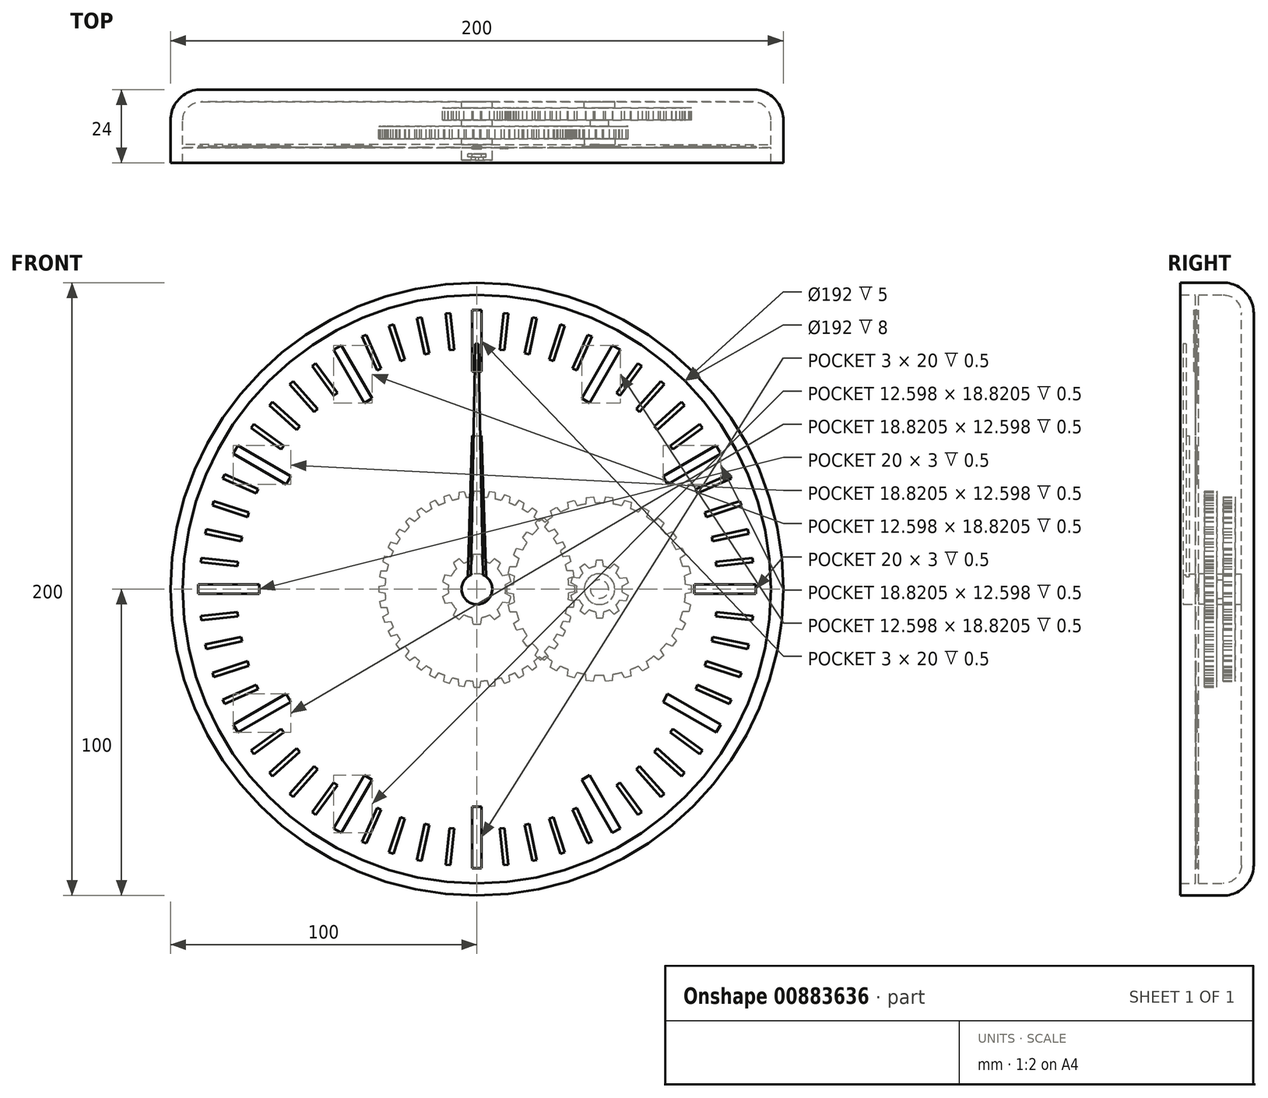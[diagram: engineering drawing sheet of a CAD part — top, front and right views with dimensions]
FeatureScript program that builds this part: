
annotation { "Feature Type Name" : "Feature", "Feature Type Description" : "" }
export const myFeature = defineFeature(function(context is Context, id is Id, definition is map)
    precondition{}
    {
        {
            var Q0;
            Q0=qCreatedBy(makeId("Front.planeOp"),FACE);
            var sketch = newSketch(context, id + "F0", { "sketchPlane" : qUnion([Q0])});
            skCircle(sketch, "E0", {"center": v(0, 0) * mm, "radius": 100 * mm});
            skSolve(sketch);
        }
        {
            var Q0;
            Q0=makeQuery(id+"F0.imprint","IMPRINT",FACE,{"disambiguationData":[TD([[makeQuery(id+"F0.imprint","IMPRINT",EDGE,{"derivedFrom":sQuery(id+"F0.wireOp",EDGE,"E0")}),1.0]])]});
            extrude(context, id + "F1", {"entities" : qUnion([Q0]), "depth" : 24 * mm, "offsetDistance" : 25 * mm});
        }
        {
            var Q0;
            Q0=makeQuery(id+"F1.opExtrude","CAP_EDGE",EDGE,{"disambiguationData":[OSD([sQuery(id+"F0.wireOp",EDGE,"E0")])],"isStart":true});
            fillet(context, id + "F2", {"entities" : qUnion([Q0]), "radius" : 10 * mm, "tangentPropagation" : true, "allowEdgeOverflow" : false});
        }
        {
            var Q0;
            Q0=makeQuery(id+"F1.opExtrude","CAP_FACE",FACE,{"disambiguationData":[OSD([sQuery(id+"F0.wireOp",EDGE,"E0")])],"isStart":false});
            shell(context, id + "F3", {"entities" : qUnion([Q0]), "thickness" : 4 * mm});
        }
        {
            var Q0;
            {var subQ0=sQuery(id+"F0.wireOp",EDGE,"E0");Q0=makeQuery(id+"F3.opShell","OFFSET_FACE",FACE,{"disambiguationData":[OSD([subQ0]),TDD([makeQuery(id+"F1.opExtrude","CAP_FACE",FACE,{"disambiguationData":[OSD([subQ0])],"isStart":true})])]});}
            var sketch = newSketch(context, id + "F4", { "sketchPlane" : qUnion([Q0])});
            skCircle(sketch, "E1", {"center": v(0, 0) * mm, "radius": 3 * mm});
            skCircle(sketch, "E2", {"center": v(0, 0) * mm, "radius": 5 * mm});
            skCircle(sketch, "E3", {"center": v(40, 0) * mm, "radius": 3 * mm});
            skCircle(sketch, "E4", {"center": v(40, 0) * mm, "radius": 5 * mm});
            skSolve(sketch);
        }
        {
            var Q0;
            Q0 = qSketchRegion(id + "F4", true);
            extrude(context, id + "F5", {"entities" : qUnion([Q0]), "operationType" : NewBodyOperationType.ADD, "depth" : 2 * mm, "offsetDistance" : 25 * mm});
        }
        {
            var Q0;
            {var subQ0=sQuery(id+"F0.wireOp",EDGE,"E0");Q0=makeQuery(id+"F5.boolean.opBoolean","SPLIT",FACE,{"disambiguationData":[TD([makeQuery(id+"F5.opExtrude","SWEPT_FACE",FACE,{"disambiguationData":[OSD([sQuery(id+"F4.wireOp",EDGE,"E1")])]})])],"derivedFrom":makeQuery(id+"F3.opShell","OFFSET_FACE",FACE,{"disambiguationData":[OSD([subQ0]),TDD([makeQuery(id+"F1.opExtrude","CAP_FACE",FACE,{"disambiguationData":[OSD([subQ0])],"isStart":true})])]})});}
            extrude(context, id + "F6", {"entities" : qUnion([Q0]), "depth" : 19 * mm, "offsetDistance" : 25 * mm});
        }
        {
            var Q0;
            {var subQ0=sQuery(id+"F0.wireOp",EDGE,"E0");Q0=makeQuery(id+"F5.boolean.opBoolean","SPLIT",FACE,{"disambiguationData":[TD([makeQuery(id+"F5.opExtrude","SWEPT_FACE",FACE,{"disambiguationData":[OSD([sQuery(id+"F4.wireOp",EDGE,"E3")])]})])],"derivedFrom":makeQuery(id+"F3.opShell","OFFSET_FACE",FACE,{"disambiguationData":[OSD([subQ0]),TDD([makeQuery(id+"F1.opExtrude","CAP_FACE",FACE,{"disambiguationData":[OSD([subQ0])],"isStart":true})])]})});}
            extrude(context, id + "F7", {"entities" : qUnion([Q0]), "depth" : 8 * mm, "offsetDistance" : 25 * mm});
        }
        {
            var Q0;
            Q0=makeQuery(id+"F5.opExtrude","CAP_FACE",FACE,{"disambiguationData":[OSD([sQuery(id+"F4.wireOp",EDGE,"E1"),sQuery(id+"F4.wireOp",EDGE,"E2")])],"isStart":false});
            var sketch = newSketch(context, id + "F8", { "sketchPlane" : qUnion([Q0])});
            skCircle(sketch, "E5", {"center": v(0, 0) * mm, "radius": 9.38 * mm});
            skLineSegment(sketch, "E6", {"start": v(0, 11.38) * mm, "end": v(1.18, 11.38) * mm});
            skLineSegment(sketch, "E7", {"start": v(1.18, 11.38) * mm, "end": v(1.55, 9.25) * mm});
            skLineSegment(sketch, "E8.MirrorCS", {"start": v(0, 11.38) * mm, "end": v(-1.18, 11.38) * mm});
            skLineSegment(sketch, "E9.MirrorCS", {"start": v(-1.18, 11.38) * mm, "end": v(-1.55, 9.25) * mm});
            skLineSegment(sketch, "E10.1.0", {"start": v(-7.64, 8.51) * mm, "end": v(-6.7, 6.57) * mm});
            skLineSegment(sketch, "E10.1.1", {"start": v(-6.69, 9.2) * mm, "end": v(-7.64, 8.51) * mm});
            skLineSegment(sketch, "E10.1.2", {"start": v(-6.69, 9.2) * mm, "end": v(-5.73, 9.9) * mm});
            skLineSegment(sketch, "E10.1.3", {"start": v(-5.73, 9.9) * mm, "end": v(-4.18, 8.4) * mm});
            skLineSegment(sketch, "E10.2.0", {"start": v(-11.18, 2.4) * mm, "end": v(-9.27, 1.38) * mm});
            skLineSegment(sketch, "E10.2.1", {"start": v(-10.82, 3.52) * mm, "end": v(-11.18, 2.4) * mm});
            skLineSegment(sketch, "E10.2.2", {"start": v(-10.82, 3.52) * mm, "end": v(-10.45, 4.64) * mm});
            skLineSegment(sketch, "E10.2.3", {"start": v(-10.45, 4.64) * mm, "end": v(-8.31, 4.33) * mm});
            skLineSegment(sketch, "E11.2.3.0", {"start": v(-10.45, -4.64) * mm, "end": v(-8.31, -4.33) * mm});
            skLineSegment(sketch, "E11.3.3.0", {"start": v(-10.82, -3.52) * mm, "end": v(-10.45, -4.64) * mm});
            skLineSegment(sketch, "E11.6.3.0", {"start": v(-10.82, -3.52) * mm, "end": v(-11.18, -2.4) * mm});
            skLineSegment(sketch, "E11.9.3.0", {"start": v(-11.18, -2.4) * mm, "end": v(-9.27, -1.38) * mm});
            skLineSegment(sketch, "E11.2.4.0", {"start": v(-5.73, -9.9) * mm, "end": v(-4.18, -8.4) * mm});
            skLineSegment(sketch, "E11.3.4.0", {"start": v(-6.69, -9.2) * mm, "end": v(-5.73, -9.9) * mm});
            skLineSegment(sketch, "E11.6.4.0", {"start": v(-6.69, -9.2) * mm, "end": v(-7.64, -8.51) * mm});
            skLineSegment(sketch, "E11.9.4.0", {"start": v(-7.64, -8.51) * mm, "end": v(-6.7, -6.57) * mm});
            skLineSegment(sketch, "E11.2.5.0", {"start": v(1.18, -11.38) * mm, "end": v(1.55, -9.25) * mm});
            skLineSegment(sketch, "E11.3.5.0", {"start": v(0, -11.38) * mm, "end": v(1.18, -11.38) * mm});
            skLineSegment(sketch, "E11.6.5.0", {"start": v(0, -11.38) * mm, "end": v(-1.18, -11.38) * mm});
            skLineSegment(sketch, "E11.9.5.0", {"start": v(-1.18, -11.38) * mm, "end": v(-1.55, -9.25) * mm});
            skLineSegment(sketch, "E11.2.6.0", {"start": v(7.64, -8.51) * mm, "end": v(6.7, -6.57) * mm});
            skLineSegment(sketch, "E11.3.6.0", {"start": v(6.69, -9.2) * mm, "end": v(7.64, -8.51) * mm});
            skLineSegment(sketch, "E11.6.6.0", {"start": v(6.69, -9.2) * mm, "end": v(5.73, -9.9) * mm});
            skLineSegment(sketch, "E11.9.6.0", {"start": v(5.73, -9.9) * mm, "end": v(4.18, -8.4) * mm});
            skLineSegment(sketch, "E11.2.7.0", {"start": v(11.18, -2.4) * mm, "end": v(9.27, -1.38) * mm});
            skLineSegment(sketch, "E11.3.7.0", {"start": v(10.82, -3.52) * mm, "end": v(11.18, -2.4) * mm});
            skLineSegment(sketch, "E11.6.7.0", {"start": v(10.82, -3.52) * mm, "end": v(10.45, -4.64) * mm});
            skLineSegment(sketch, "E11.9.7.0", {"start": v(10.45, -4.64) * mm, "end": v(8.31, -4.33) * mm});
            skLineSegment(sketch, "E11.2.8.0", {"start": v(10.45, 4.64) * mm, "end": v(8.31, 4.33) * mm});
            skLineSegment(sketch, "E11.3.8.0", {"start": v(10.82, 3.52) * mm, "end": v(10.45, 4.64) * mm});
            skLineSegment(sketch, "E11.6.8.0", {"start": v(10.82, 3.52) * mm, "end": v(11.18, 2.4) * mm});
            skLineSegment(sketch, "E11.9.8.0", {"start": v(11.18, 2.4) * mm, "end": v(9.27, 1.38) * mm});
            skLineSegment(sketch, "E11.2.9.0", {"start": v(5.73, 9.9) * mm, "end": v(4.18, 8.4) * mm});
            skLineSegment(sketch, "E11.3.9.0", {"start": v(6.69, 9.2) * mm, "end": v(5.73, 9.9) * mm});
            skLineSegment(sketch, "E11.6.9.0", {"start": v(6.69, 9.2) * mm, "end": v(7.64, 8.51) * mm});
            skLineSegment(sketch, "E11.9.9.0", {"start": v(7.64, 8.51) * mm, "end": v(6.7, 6.57) * mm});
            skSolve(sketch);
        }
        {
            var Q0;
            Q0 = qSketchRegion(id + "F8", true);
            extrude(context, id + "F9", {"entities" : qUnion([Q0]), "operationType" : NewBodyOperationType.ADD, "depth" : 4 * mm, "offsetDistance" : 25 * mm});
        }
        {
            var Q0;
            Q0=makeQuery(id+"F5.opExtrude","CAP_FACE",FACE,{"disambiguationData":[OSD([sQuery(id+"F4.wireOp",EDGE,"E3"),sQuery(id+"F4.wireOp",EDGE,"E4")])],"isStart":false});
            var sketch = newSketch(context, id + "F10", { "sketchPlane" : qUnion([Q0])});
            skCircle(sketch, "E12", {"center": v(40, 0) * mm, "radius": 28.12 * mm});
            skLineSegment(sketch, "E13", {"start": v(9.88, 0) * mm, "end": v(9.88, 1.18) * mm});
            skLineSegment(sketch, "E14", {"start": v(9.88, 1.18) * mm, "end": v(11.92, 1.54) * mm});
            skLineSegment(sketch, "E15.MirrorCS", {"start": v(9.88, 0) * mm, "end": v(9.88, -1.18) * mm});
            skLineSegment(sketch, "E16.MirrorCS", {"start": v(9.88, -1.18) * mm, "end": v(11.92, -1.54) * mm});
            skLineSegment(sketch, "E17.1.0", {"start": v(10.29, -5.11) * mm, "end": v(12.21, -4.33) * mm});
            skLineSegment(sketch, "E17.1.1", {"start": v(10.53, -6.26) * mm, "end": v(10.29, -5.11) * mm});
            skLineSegment(sketch, "E17.1.2", {"start": v(10.53, -6.26) * mm, "end": v(10.78, -7.42) * mm});
            skLineSegment(sketch, "E17.1.3", {"start": v(10.78, -7.42) * mm, "end": v(12.85, -7.34) * mm});
            skLineSegment(sketch, "E17.2.0", {"start": v(12, -11.18) * mm, "end": v(13.72, -10.02) * mm});
            skLineSegment(sketch, "E17.2.1", {"start": v(12.48, -12.25) * mm, "end": v(12, -11.18) * mm});
            skLineSegment(sketch, "E17.2.2", {"start": v(12.48, -12.25) * mm, "end": v(12.96, -13.33) * mm});
            skLineSegment(sketch, "E17.2.3", {"start": v(12.96, -13.33) * mm, "end": v(14.97, -12.83) * mm});
            skLineSegment(sketch, "E18.1.3.0", {"start": v(14.94, -16.75) * mm, "end": v(16.38, -15.26) * mm});
            skLineSegment(sketch, "E18.3.3.0", {"start": v(15.63, -17.7) * mm, "end": v(14.94, -16.75) * mm});
            skLineSegment(sketch, "E18.6.3.0", {"start": v(15.63, -17.7) * mm, "end": v(16.32, -18.66) * mm});
            skLineSegment(sketch, "E18.9.3.0", {"start": v(16.32, -18.66) * mm, "end": v(18.18, -17.75) * mm});
            skLineSegment(sketch, "E18.1.4.0", {"start": v(18.97, -21.6) * mm, "end": v(20.07, -19.84) * mm});
            skLineSegment(sketch, "E18.3.4.0", {"start": v(19.84, -22.39) * mm, "end": v(18.97, -21.6) * mm});
            skLineSegment(sketch, "E18.6.4.0", {"start": v(19.84, -22.39) * mm, "end": v(20.72, -23.18) * mm});
            skLineSegment(sketch, "E18.9.4.0", {"start": v(20.72, -23.18) * mm, "end": v(22.35, -21.9) * mm});
            skLineSegment(sketch, "E18.1.5.0", {"start": v(23.92, -25.5) * mm, "end": v(24.63, -23.55) * mm});
            skLineSegment(sketch, "E18.3.5.0", {"start": v(24.94, -26.09) * mm, "end": v(23.92, -25.5) * mm});
            skLineSegment(sketch, "E18.6.5.0", {"start": v(24.94, -26.09) * mm, "end": v(25.96, -26.68) * mm});
            skLineSegment(sketch, "E18.9.5.0", {"start": v(25.96, -26.68) * mm, "end": v(27.3, -25.09) * mm});
            skLineSegment(sketch, "E18.1.6.0", {"start": v(29.57, -28.29) * mm, "end": v(29.86, -26.23) * mm});
            skLineSegment(sketch, "E18.3.6.0", {"start": v(30.7, -28.65) * mm, "end": v(29.57, -28.29) * mm});
            skLineSegment(sketch, "E18.6.6.0", {"start": v(30.7, -28.65) * mm, "end": v(31.81, -29.01) * mm});
            skLineSegment(sketch, "E18.9.6.0", {"start": v(31.81, -29.01) * mm, "end": v(32.78, -27.18) * mm});
            skLineSegment(sketch, "E18.1.7.0", {"start": v(35.68, -29.84) * mm, "end": v(35.53, -27.77) * mm});
            skLineSegment(sketch, "E18.3.7.0", {"start": v(36.85, -29.96) * mm, "end": v(35.68, -29.84) * mm});
            skLineSegment(sketch, "E18.6.7.0", {"start": v(36.85, -29.96) * mm, "end": v(38.02, -30.08) * mm});
            skLineSegment(sketch, "E18.9.7.0", {"start": v(38.02, -30.08) * mm, "end": v(38.6, -28.09) * mm});
            skLineSegment(sketch, "E18.1.8.0", {"start": v(41.98, -30.08) * mm, "end": v(41.4, -28.09) * mm});
            skLineSegment(sketch, "E18.3.8.0", {"start": v(43.15, -29.96) * mm, "end": v(41.98, -30.08) * mm});
            skLineSegment(sketch, "E18.6.8.0", {"start": v(43.15, -29.96) * mm, "end": v(44.32, -29.84) * mm});
            skLineSegment(sketch, "E18.9.8.0", {"start": v(44.32, -29.84) * mm, "end": v(44.47, -27.77) * mm});
            skLineSegment(sketch, "E18.1.9.0", {"start": v(48.19, -29.01) * mm, "end": v(47.22, -27.18) * mm});
            skLineSegment(sketch, "E18.3.9.0", {"start": v(49.3, -28.65) * mm, "end": v(48.19, -29.01) * mm});
            skLineSegment(sketch, "E18.6.9.0", {"start": v(49.3, -28.65) * mm, "end": v(50.43, -28.29) * mm});
            skLineSegment(sketch, "E18.9.9.0", {"start": v(50.43, -28.29) * mm, "end": v(50.14, -26.23) * mm});
            skLineSegment(sketch, "E18.1.10.0", {"start": v(54.04, -26.68) * mm, "end": v(52.7, -25.09) * mm});
            skLineSegment(sketch, "E18.3.10.0", {"start": v(55.06, -26.09) * mm, "end": v(54.04, -26.68) * mm});
            skLineSegment(sketch, "E18.6.10.0", {"start": v(55.06, -26.09) * mm, "end": v(56.08, -25.5) * mm});
            skLineSegment(sketch, "E18.9.10.0", {"start": v(56.08, -25.5) * mm, "end": v(55.37, -23.55) * mm});
            skLineSegment(sketch, "E18.1.11.0", {"start": v(59.28, -23.18) * mm, "end": v(57.65, -21.9) * mm});
            skLineSegment(sketch, "E18.3.11.0", {"start": v(60.16, -22.39) * mm, "end": v(59.28, -23.18) * mm});
            skLineSegment(sketch, "E18.6.11.0", {"start": v(60.16, -22.39) * mm, "end": v(61.03, -21.6) * mm});
            skLineSegment(sketch, "E18.9.11.0", {"start": v(61.03, -21.6) * mm, "end": v(59.93, -19.84) * mm});
            skLineSegment(sketch, "E18.1.12.0", {"start": v(63.68, -18.66) * mm, "end": v(61.82, -17.75) * mm});
            skLineSegment(sketch, "E18.3.12.0", {"start": v(64.37, -17.7) * mm, "end": v(63.68, -18.66) * mm});
            skLineSegment(sketch, "E18.6.12.0", {"start": v(64.37, -17.7) * mm, "end": v(65.06, -16.75) * mm});
            skLineSegment(sketch, "E18.9.12.0", {"start": v(65.06, -16.75) * mm, "end": v(63.62, -15.26) * mm});
            skLineSegment(sketch, "E18.1.13.0", {"start": v(67.04, -13.33) * mm, "end": v(65.03, -12.83) * mm});
            skLineSegment(sketch, "E18.3.13.0", {"start": v(67.52, -12.25) * mm, "end": v(67.04, -13.33) * mm});
            skLineSegment(sketch, "E18.6.13.0", {"start": v(67.52, -12.25) * mm, "end": v(68, -11.18) * mm});
            skLineSegment(sketch, "E18.9.13.0", {"start": v(68, -11.18) * mm, "end": v(66.28, -10.02) * mm});
            skLineSegment(sketch, "E18.1.14.0", {"start": v(69.22, -7.42) * mm, "end": v(67.15, -7.34) * mm});
            skLineSegment(sketch, "E18.3.14.0", {"start": v(69.47, -6.26) * mm, "end": v(69.22, -7.42) * mm});
            skLineSegment(sketch, "E18.6.14.0", {"start": v(69.47, -6.26) * mm, "end": v(69.71, -5.11) * mm});
            skLineSegment(sketch, "E18.9.14.0", {"start": v(69.71, -5.11) * mm, "end": v(67.79, -4.33) * mm});
            skLineSegment(sketch, "E18.1.15.0", {"start": v(70.13, -1.18) * mm, "end": v(68.08, -1.54) * mm});
            skLineSegment(sketch, "E18.3.15.0", {"start": v(70.12, 0) * mm, "end": v(70.12, -1.18) * mm});
            skLineSegment(sketch, "E18.6.15.0", {"start": v(70.12, 0) * mm, "end": v(70.12, 1.18) * mm});
            skLineSegment(sketch, "E18.9.15.0", {"start": v(70.13, 1.18) * mm, "end": v(68.08, 1.54) * mm});
            skLineSegment(sketch, "E18.1.16.0", {"start": v(69.71, 5.11) * mm, "end": v(67.79, 4.33) * mm});
            skLineSegment(sketch, "E18.3.16.0", {"start": v(69.47, 6.26) * mm, "end": v(69.71, 5.11) * mm});
            skLineSegment(sketch, "E18.6.16.0", {"start": v(69.47, 6.26) * mm, "end": v(69.22, 7.42) * mm});
            skLineSegment(sketch, "E18.9.16.0", {"start": v(69.22, 7.42) * mm, "end": v(67.15, 7.34) * mm});
            skLineSegment(sketch, "E18.1.17.0", {"start": v(68, 11.18) * mm, "end": v(66.28, 10.02) * mm});
            skLineSegment(sketch, "E18.3.17.0", {"start": v(67.52, 12.25) * mm, "end": v(68, 11.18) * mm});
            skLineSegment(sketch, "E18.6.17.0", {"start": v(67.52, 12.25) * mm, "end": v(67.04, 13.33) * mm});
            skLineSegment(sketch, "E18.9.17.0", {"start": v(67.04, 13.33) * mm, "end": v(65.03, 12.83) * mm});
            skLineSegment(sketch, "E18.1.18.0", {"start": v(65.06, 16.75) * mm, "end": v(63.62, 15.26) * mm});
            skLineSegment(sketch, "E18.3.18.0", {"start": v(64.37, 17.7) * mm, "end": v(65.06, 16.75) * mm});
            skLineSegment(sketch, "E18.6.18.0", {"start": v(64.37, 17.7) * mm, "end": v(63.68, 18.66) * mm});
            skLineSegment(sketch, "E18.9.18.0", {"start": v(63.68, 18.66) * mm, "end": v(61.82, 17.75) * mm});
            skLineSegment(sketch, "E18.1.19.0", {"start": v(61.03, 21.6) * mm, "end": v(59.93, 19.84) * mm});
            skLineSegment(sketch, "E18.3.19.0", {"start": v(60.16, 22.39) * mm, "end": v(61.03, 21.6) * mm});
            skLineSegment(sketch, "E18.6.19.0", {"start": v(60.16, 22.39) * mm, "end": v(59.28, 23.18) * mm});
            skLineSegment(sketch, "E18.9.19.0", {"start": v(59.28, 23.18) * mm, "end": v(57.65, 21.9) * mm});
            skLineSegment(sketch, "E18.1.20.0", {"start": v(56.08, 25.5) * mm, "end": v(55.37, 23.55) * mm});
            skLineSegment(sketch, "E18.3.20.0", {"start": v(55.06, 26.09) * mm, "end": v(56.08, 25.5) * mm});
            skLineSegment(sketch, "E18.6.20.0", {"start": v(55.06, 26.09) * mm, "end": v(54.04, 26.68) * mm});
            skLineSegment(sketch, "E18.9.20.0", {"start": v(54.04, 26.68) * mm, "end": v(52.7, 25.09) * mm});
            skLineSegment(sketch, "E18.1.21.0", {"start": v(50.43, 28.29) * mm, "end": v(50.14, 26.23) * mm});
            skLineSegment(sketch, "E18.3.21.0", {"start": v(49.3, 28.65) * mm, "end": v(50.43, 28.29) * mm});
            skLineSegment(sketch, "E18.6.21.0", {"start": v(49.3, 28.65) * mm, "end": v(48.19, 29.01) * mm});
            skLineSegment(sketch, "E18.9.21.0", {"start": v(48.19, 29.01) * mm, "end": v(47.22, 27.18) * mm});
            skLineSegment(sketch, "E18.1.22.0", {"start": v(44.32, 29.84) * mm, "end": v(44.47, 27.77) * mm});
            skLineSegment(sketch, "E18.3.22.0", {"start": v(43.15, 29.96) * mm, "end": v(44.32, 29.84) * mm});
            skLineSegment(sketch, "E18.6.22.0", {"start": v(43.15, 29.96) * mm, "end": v(41.98, 30.08) * mm});
            skLineSegment(sketch, "E18.9.22.0", {"start": v(41.98, 30.08) * mm, "end": v(41.4, 28.09) * mm});
            skLineSegment(sketch, "E18.1.23.0", {"start": v(38.02, 30.08) * mm, "end": v(38.6, 28.09) * mm});
            skLineSegment(sketch, "E18.3.23.0", {"start": v(36.85, 29.96) * mm, "end": v(38.02, 30.08) * mm});
            skLineSegment(sketch, "E18.6.23.0", {"start": v(36.85, 29.96) * mm, "end": v(35.68, 29.84) * mm});
            skLineSegment(sketch, "E18.9.23.0", {"start": v(35.68, 29.84) * mm, "end": v(35.53, 27.77) * mm});
            skLineSegment(sketch, "E18.1.24.0", {"start": v(31.81, 29.01) * mm, "end": v(32.78, 27.18) * mm});
            skLineSegment(sketch, "E18.3.24.0", {"start": v(30.7, 28.65) * mm, "end": v(31.81, 29.01) * mm});
            skLineSegment(sketch, "E18.6.24.0", {"start": v(30.7, 28.65) * mm, "end": v(29.57, 28.29) * mm});
            skLineSegment(sketch, "E18.9.24.0", {"start": v(29.57, 28.29) * mm, "end": v(29.86, 26.23) * mm});
            skLineSegment(sketch, "E18.1.25.0", {"start": v(25.96, 26.68) * mm, "end": v(27.3, 25.09) * mm});
            skLineSegment(sketch, "E18.3.25.0", {"start": v(24.94, 26.09) * mm, "end": v(25.96, 26.68) * mm});
            skLineSegment(sketch, "E18.6.25.0", {"start": v(24.94, 26.09) * mm, "end": v(23.92, 25.5) * mm});
            skLineSegment(sketch, "E18.9.25.0", {"start": v(23.92, 25.5) * mm, "end": v(24.63, 23.55) * mm});
            skLineSegment(sketch, "E18.1.26.0", {"start": v(20.72, 23.18) * mm, "end": v(22.35, 21.9) * mm});
            skLineSegment(sketch, "E18.3.26.0", {"start": v(19.84, 22.39) * mm, "end": v(20.72, 23.18) * mm});
            skLineSegment(sketch, "E18.6.26.0", {"start": v(19.84, 22.39) * mm, "end": v(18.97, 21.6) * mm});
            skLineSegment(sketch, "E18.9.26.0", {"start": v(18.97, 21.6) * mm, "end": v(20.07, 19.84) * mm});
            skLineSegment(sketch, "E18.1.27.0", {"start": v(16.32, 18.66) * mm, "end": v(18.18, 17.75) * mm});
            skLineSegment(sketch, "E18.3.27.0", {"start": v(15.63, 17.7) * mm, "end": v(16.32, 18.66) * mm});
            skLineSegment(sketch, "E18.6.27.0", {"start": v(15.63, 17.7) * mm, "end": v(14.94, 16.75) * mm});
            skLineSegment(sketch, "E18.9.27.0", {"start": v(14.94, 16.75) * mm, "end": v(16.38, 15.26) * mm});
            skLineSegment(sketch, "E18.1.28.0", {"start": v(12.96, 13.33) * mm, "end": v(14.97, 12.83) * mm});
            skLineSegment(sketch, "E18.3.28.0", {"start": v(12.48, 12.25) * mm, "end": v(12.96, 13.33) * mm});
            skLineSegment(sketch, "E18.6.28.0", {"start": v(12.48, 12.25) * mm, "end": v(12, 11.18) * mm});
            skLineSegment(sketch, "E18.9.28.0", {"start": v(12, 11.18) * mm, "end": v(13.72, 10.02) * mm});
            skLineSegment(sketch, "E18.1.29.0", {"start": v(10.78, 7.42) * mm, "end": v(12.85, 7.34) * mm});
            skLineSegment(sketch, "E18.3.29.0", {"start": v(10.53, 6.26) * mm, "end": v(10.78, 7.42) * mm});
            skLineSegment(sketch, "E18.6.29.0", {"start": v(10.53, 6.26) * mm, "end": v(10.29, 5.11) * mm});
            skLineSegment(sketch, "E18.9.29.0", {"start": v(10.29, 5.11) * mm, "end": v(12.21, 4.33) * mm});
            skSolve(sketch);
        }
        {
            var Q0;
            Q0 = qSketchRegion(id + "F10", true);
            extrude(context, id + "F11", {"entities" : qUnion([Q0]), "operationType" : NewBodyOperationType.ADD, "depth" : 4 * mm, "offsetDistance" : 25 * mm});
        }
        {
            var Q0;
            Q0=makeQuery(id+"F9.opExtrude","CAP_FACE",FACE,{"disambiguationData":[OSD([sQuery(id+"F8.wireOp",EDGE,"E5"),sQuery(id+"F8.wireOp",EDGE,"E6"),sQuery(id+"F8.wireOp",EDGE,"E7"),sQuery(id+"F8.wireOp",EDGE,"E8.MirrorCS"),sQuery(id+"F8.wireOp",EDGE,"E9.MirrorCS"),sQuery(id+"F8.wireOp",EDGE,"E10.1.0"),sQuery(id+"F8.wireOp",EDGE,"E10.1.1"),sQuery(id+"F8.wireOp",EDGE,"E10.1.2"),sQuery(id+"F8.wireOp",EDGE,"E10.1.3"),sQuery(id+"F8.wireOp",EDGE,"E10.2.0"),sQuery(id+"F8.wireOp",EDGE,"E10.2.1"),sQuery(id+"F8.wireOp",EDGE,"E10.2.2"),sQuery(id+"F8.wireOp",EDGE,"E10.2.3"),sQuery(id+"F8.wireOp",EDGE,"E11.2.3.0"),sQuery(id+"F8.wireOp",EDGE,"E11.3.3.0"),sQuery(id+"F8.wireOp",EDGE,"E11.6.3.0"),sQuery(id+"F8.wireOp",EDGE,"E11.9.3.0"),sQuery(id+"F8.wireOp",EDGE,"E11.2.4.0"),sQuery(id+"F8.wireOp",EDGE,"E11.3.4.0"),sQuery(id+"F8.wireOp",EDGE,"E11.6.4.0"),sQuery(id+"F8.wireOp",EDGE,"E11.9.4.0"),sQuery(id+"F8.wireOp",EDGE,"E11.2.5.0"),sQuery(id+"F8.wireOp",EDGE,"E11.3.5.0"),sQuery(id+"F8.wireOp",EDGE,"E11.6.5.0"),sQuery(id+"F8.wireOp",EDGE,"E11.9.5.0"),sQuery(id+"F8.wireOp",EDGE,"E11.2.6.0"),sQuery(id+"F8.wireOp",EDGE,"E11.3.6.0"),sQuery(id+"F8.wireOp",EDGE,"E11.6.6.0"),sQuery(id+"F8.wireOp",EDGE,"E11.9.6.0"),sQuery(id+"F8.wireOp",EDGE,"E11.2.7.0"),sQuery(id+"F8.wireOp",EDGE,"E11.3.7.0"),sQuery(id+"F8.wireOp",EDGE,"E11.6.7.0"),sQuery(id+"F8.wireOp",EDGE,"E11.9.7.0"),sQuery(id+"F8.wireOp",EDGE,"E11.2.8.0"),sQuery(id+"F8.wireOp",EDGE,"E11.3.8.0"),sQuery(id+"F8.wireOp",EDGE,"E11.6.8.0"),sQuery(id+"F8.wireOp",EDGE,"E11.9.8.0"),sQuery(id+"F8.wireOp",EDGE,"E11.2.9.0"),sQuery(id+"F8.wireOp",EDGE,"E11.3.9.0"),sQuery(id+"F8.wireOp",EDGE,"E11.6.9.0"),sQuery(id+"F8.wireOp",EDGE,"E11.9.9.0")])],"isStart":false});
            var sketch = newSketch(context, id + "F12", { "sketchPlane" : qUnion([Q0])});
            skCircle(sketch, "E19.0", {"center": v(0, 0) * mm, "radius": 3 * mm});
            skCircle(sketch, "E20.0", {"center": v(0, 0) * mm, "radius": 5 * mm});
            skSolve(sketch);
        }
        {
            var Q0;
            Q0 = qSketchRegion(id + "F12", true);
            extrude(context, id + "F13", {"entities" : qUnion([Q0]), "depth" : 2 * mm, "offsetDistance" : 25 * mm});
        }
        {
            var Q0;
            Q0=makeQuery(id+"F13.opExtrude","CAP_FACE",FACE,{"disambiguationData":[OSD([sQuery(id+"F12.wireOp",EDGE,"E19.0"),sQuery(id+"F12.wireOp",EDGE,"E20.0")])],"isStart":false});
            var sketch = newSketch(context, id + "F14", { "sketchPlane" : qUnion([Q0])});
            skCircle(sketch, "E21.0", {"center": v(0, 0) * mm, "radius": 3 * mm});
            skCircle(sketch, "E22", {"center": v(0, 0) * mm, "radius": 30 * mm});
            skLineSegment(sketch, "E23", {"start": v(0, 32) * mm, "end": v(0.94, 32) * mm});
            skLineSegment(sketch, "E24", {"start": v(0.94, 32) * mm, "end": v(1.3, 29.97) * mm});
            skLineSegment(sketch, "E25.MirrorCS", {"start": v(0, 32) * mm, "end": v(-0.94, 32) * mm});
            skLineSegment(sketch, "E26.MirrorCS", {"start": v(-0.94, 32) * mm, "end": v(-1.3, 29.97) * mm});
            skLineSegment(sketch, "E27.1.0", {"start": v(-5.94, 31.46) * mm, "end": v(-5.97, 29.4) * mm});
            skLineSegment(sketch, "E27.1.1", {"start": v(-5, 31.6) * mm, "end": v(-5.94, 31.46) * mm});
            skLineSegment(sketch, "E27.1.2", {"start": v(-5, 31.6) * mm, "end": v(-4.08, 31.75) * mm});
            skLineSegment(sketch, "E27.1.3", {"start": v(-4.08, 31.75) * mm, "end": v(-3.4, 29.8) * mm});
            skLineSegment(sketch, "E27.2.0", {"start": v(-10.78, 30.14) * mm, "end": v(-10.5, 28.1) * mm});
            skLineSegment(sketch, "E27.2.1", {"start": v(-9.89, 30.43) * mm, "end": v(-10.78, 30.14) * mm});
            skLineSegment(sketch, "E27.2.2", {"start": v(-9.89, 30.43) * mm, "end": v(-9, 30.73) * mm});
            skLineSegment(sketch, "E27.2.3", {"start": v(-9, 30.73) * mm, "end": v(-8.03, 28.9) * mm});
            skLineSegment(sketch, "E28.2.3.0", {"start": v(-15.37, 28.08) * mm, "end": v(-14.77, 26.11) * mm});
            skLineSegment(sketch, "E28.3.3.0", {"start": v(-14.53, 28.51) * mm, "end": v(-15.37, 28.08) * mm});
            skLineSegment(sketch, "E28.6.3.0", {"start": v(-14.53, 28.51) * mm, "end": v(-13.69, 28.94) * mm});
            skLineSegment(sketch, "E28.9.3.0", {"start": v(-13.69, 28.94) * mm, "end": v(-12.45, 27.3) * mm});
            skLineSegment(sketch, "E28.2.4.0", {"start": v(-19.57, 25.33) * mm, "end": v(-18.67, 23.48) * mm});
            skLineSegment(sketch, "E28.3.4.0", {"start": v(-18.8, 25.89) * mm, "end": v(-19.57, 25.33) * mm});
            skLineSegment(sketch, "E28.6.4.0", {"start": v(-18.8, 25.89) * mm, "end": v(-18.05, 26.44) * mm});
            skLineSegment(sketch, "E28.9.4.0", {"start": v(-18.05, 26.44) * mm, "end": v(-16.57, 25.01) * mm});
            skLineSegment(sketch, "E28.2.5.0", {"start": v(-23.3, 21.96) * mm, "end": v(-22.11, 20.27) * mm});
            skLineSegment(sketch, "E28.3.5.0", {"start": v(-22.63, 22.63) * mm, "end": v(-23.3, 21.96) * mm});
            skLineSegment(sketch, "E28.6.5.0", {"start": v(-22.63, 22.63) * mm, "end": v(-21.96, 23.3) * mm});
            skLineSegment(sketch, "E28.9.5.0", {"start": v(-21.96, 23.3) * mm, "end": v(-20.27, 22.11) * mm});
            skLineSegment(sketch, "E28.2.6.0", {"start": v(-26.44, 18.05) * mm, "end": v(-25.01, 16.57) * mm});
            skLineSegment(sketch, "E28.3.6.0", {"start": v(-25.89, 18.8) * mm, "end": v(-26.44, 18.05) * mm});
            skLineSegment(sketch, "E28.6.6.0", {"start": v(-25.89, 18.8) * mm, "end": v(-25.33, 19.57) * mm});
            skLineSegment(sketch, "E28.9.6.0", {"start": v(-25.33, 19.57) * mm, "end": v(-23.48, 18.67) * mm});
            skLineSegment(sketch, "E28.2.7.0", {"start": v(-28.94, 13.69) * mm, "end": v(-27.3, 12.45) * mm});
            skLineSegment(sketch, "E28.3.7.0", {"start": v(-28.51, 14.53) * mm, "end": v(-28.94, 13.69) * mm});
            skLineSegment(sketch, "E28.6.7.0", {"start": v(-28.51, 14.53) * mm, "end": v(-28.08, 15.37) * mm});
            skLineSegment(sketch, "E28.9.7.0", {"start": v(-28.08, 15.37) * mm, "end": v(-26.11, 14.77) * mm});
            skLineSegment(sketch, "E28.2.8.0", {"start": v(-30.73, 9) * mm, "end": v(-28.9, 8.03) * mm});
            skLineSegment(sketch, "E28.3.8.0", {"start": v(-30.43, 9.89) * mm, "end": v(-30.73, 9) * mm});
            skLineSegment(sketch, "E28.6.8.0", {"start": v(-30.43, 9.89) * mm, "end": v(-30.14, 10.78) * mm});
            skLineSegment(sketch, "E28.9.8.0", {"start": v(-30.14, 10.78) * mm, "end": v(-28.1, 10.5) * mm});
            skLineSegment(sketch, "E28.2.9.0", {"start": v(-31.75, 4.08) * mm, "end": v(-29.8, 3.4) * mm});
            skLineSegment(sketch, "E28.3.9.0", {"start": v(-31.6, 5) * mm, "end": v(-31.75, 4.08) * mm});
            skLineSegment(sketch, "E28.6.9.0", {"start": v(-31.6, 5) * mm, "end": v(-31.46, 5.94) * mm});
            skLineSegment(sketch, "E28.9.9.0", {"start": v(-31.46, 5.94) * mm, "end": v(-29.4, 5.97) * mm});
            skLineSegment(sketch, "E28.2.10.0", {"start": v(-32, -0.94) * mm, "end": v(-29.97, -1.3) * mm});
            skLineSegment(sketch, "E28.3.10.0", {"start": v(-32, 0) * mm, "end": v(-32, -0.94) * mm});
            skLineSegment(sketch, "E28.6.10.0", {"start": v(-32, 0) * mm, "end": v(-32, 0.94) * mm});
            skLineSegment(sketch, "E28.9.10.0", {"start": v(-32, 0.94) * mm, "end": v(-29.97, 1.3) * mm});
            skLineSegment(sketch, "E28.2.11.0", {"start": v(-31.46, -5.94) * mm, "end": v(-29.4, -5.97) * mm});
            skLineSegment(sketch, "E28.3.11.0", {"start": v(-31.6, -5) * mm, "end": v(-31.46, -5.94) * mm});
            skLineSegment(sketch, "E28.6.11.0", {"start": v(-31.6, -5) * mm, "end": v(-31.75, -4.08) * mm});
            skLineSegment(sketch, "E28.9.11.0", {"start": v(-31.75, -4.08) * mm, "end": v(-29.8, -3.4) * mm});
            skLineSegment(sketch, "E28.2.12.0", {"start": v(-30.14, -10.78) * mm, "end": v(-28.1, -10.5) * mm});
            skLineSegment(sketch, "E28.3.12.0", {"start": v(-30.43, -9.89) * mm, "end": v(-30.14, -10.78) * mm});
            skLineSegment(sketch, "E28.6.12.0", {"start": v(-30.43, -9.89) * mm, "end": v(-30.73, -9) * mm});
            skLineSegment(sketch, "E28.9.12.0", {"start": v(-30.73, -9) * mm, "end": v(-28.9, -8.03) * mm});
            skLineSegment(sketch, "E28.2.13.0", {"start": v(-28.08, -15.37) * mm, "end": v(-26.11, -14.77) * mm});
            skLineSegment(sketch, "E28.3.13.0", {"start": v(-28.51, -14.53) * mm, "end": v(-28.08, -15.37) * mm});
            skLineSegment(sketch, "E28.6.13.0", {"start": v(-28.51, -14.53) * mm, "end": v(-28.94, -13.69) * mm});
            skLineSegment(sketch, "E28.9.13.0", {"start": v(-28.94, -13.69) * mm, "end": v(-27.3, -12.45) * mm});
            skLineSegment(sketch, "E28.2.14.0", {"start": v(-25.33, -19.57) * mm, "end": v(-23.48, -18.67) * mm});
            skLineSegment(sketch, "E28.3.14.0", {"start": v(-25.89, -18.8) * mm, "end": v(-25.33, -19.57) * mm});
            skLineSegment(sketch, "E28.6.14.0", {"start": v(-25.89, -18.8) * mm, "end": v(-26.44, -18.05) * mm});
            skLineSegment(sketch, "E28.9.14.0", {"start": v(-26.44, -18.05) * mm, "end": v(-25.01, -16.57) * mm});
            skLineSegment(sketch, "E28.2.15.0", {"start": v(-21.96, -23.3) * mm, "end": v(-20.27, -22.11) * mm});
            skLineSegment(sketch, "E28.3.15.0", {"start": v(-22.63, -22.63) * mm, "end": v(-21.96, -23.3) * mm});
            skLineSegment(sketch, "E28.6.15.0", {"start": v(-22.63, -22.63) * mm, "end": v(-23.3, -21.96) * mm});
            skLineSegment(sketch, "E28.9.15.0", {"start": v(-23.3, -21.96) * mm, "end": v(-22.11, -20.27) * mm});
            skLineSegment(sketch, "E28.2.16.0", {"start": v(-18.05, -26.44) * mm, "end": v(-16.57, -25.01) * mm});
            skLineSegment(sketch, "E28.3.16.0", {"start": v(-18.8, -25.89) * mm, "end": v(-18.05, -26.44) * mm});
            skLineSegment(sketch, "E28.6.16.0", {"start": v(-18.8, -25.89) * mm, "end": v(-19.57, -25.33) * mm});
            skLineSegment(sketch, "E28.9.16.0", {"start": v(-19.57, -25.33) * mm, "end": v(-18.67, -23.48) * mm});
            skLineSegment(sketch, "E28.2.17.0", {"start": v(-13.69, -28.94) * mm, "end": v(-12.45, -27.3) * mm});
            skLineSegment(sketch, "E28.3.17.0", {"start": v(-14.53, -28.51) * mm, "end": v(-13.69, -28.94) * mm});
            skLineSegment(sketch, "E28.6.17.0", {"start": v(-14.53, -28.51) * mm, "end": v(-15.37, -28.08) * mm});
            skLineSegment(sketch, "E28.9.17.0", {"start": v(-15.37, -28.08) * mm, "end": v(-14.77, -26.11) * mm});
            skLineSegment(sketch, "E28.2.18.0", {"start": v(-9, -30.73) * mm, "end": v(-8.03, -28.9) * mm});
            skLineSegment(sketch, "E28.3.18.0", {"start": v(-9.89, -30.43) * mm, "end": v(-9, -30.73) * mm});
            skLineSegment(sketch, "E28.6.18.0", {"start": v(-9.89, -30.43) * mm, "end": v(-10.78, -30.14) * mm});
            skLineSegment(sketch, "E28.9.18.0", {"start": v(-10.78, -30.14) * mm, "end": v(-10.5, -28.1) * mm});
            skLineSegment(sketch, "E28.2.19.0", {"start": v(-4.08, -31.75) * mm, "end": v(-3.4, -29.8) * mm});
            skLineSegment(sketch, "E28.3.19.0", {"start": v(-5, -31.6) * mm, "end": v(-4.08, -31.75) * mm});
            skLineSegment(sketch, "E28.6.19.0", {"start": v(-5, -31.6) * mm, "end": v(-5.94, -31.46) * mm});
            skLineSegment(sketch, "E28.9.19.0", {"start": v(-5.94, -31.46) * mm, "end": v(-5.97, -29.4) * mm});
            skLineSegment(sketch, "E28.2.20.0", {"start": v(0.94, -32) * mm, "end": v(1.3, -29.97) * mm});
            skLineSegment(sketch, "E28.3.20.0", {"start": v(0, -32) * mm, "end": v(0.94, -32) * mm});
            skLineSegment(sketch, "E28.6.20.0", {"start": v(0, -32) * mm, "end": v(-0.94, -32) * mm});
            skLineSegment(sketch, "E28.9.20.0", {"start": v(-0.94, -32) * mm, "end": v(-1.3, -29.97) * mm});
            skLineSegment(sketch, "E28.2.21.0", {"start": v(5.94, -31.46) * mm, "end": v(5.97, -29.4) * mm});
            skLineSegment(sketch, "E28.3.21.0", {"start": v(5, -31.6) * mm, "end": v(5.94, -31.46) * mm});
            skLineSegment(sketch, "E28.6.21.0", {"start": v(5, -31.6) * mm, "end": v(4.08, -31.75) * mm});
            skLineSegment(sketch, "E28.9.21.0", {"start": v(4.08, -31.75) * mm, "end": v(3.4, -29.8) * mm});
            skLineSegment(sketch, "E28.2.22.0", {"start": v(10.78, -30.14) * mm, "end": v(10.5, -28.1) * mm});
            skLineSegment(sketch, "E28.3.22.0", {"start": v(9.89, -30.43) * mm, "end": v(10.78, -30.14) * mm});
            skLineSegment(sketch, "E28.6.22.0", {"start": v(9.89, -30.43) * mm, "end": v(9, -30.73) * mm});
            skLineSegment(sketch, "E28.9.22.0", {"start": v(9, -30.73) * mm, "end": v(8.03, -28.9) * mm});
            skLineSegment(sketch, "E28.2.23.0", {"start": v(15.37, -28.08) * mm, "end": v(14.77, -26.11) * mm});
            skLineSegment(sketch, "E28.3.23.0", {"start": v(14.53, -28.51) * mm, "end": v(15.37, -28.08) * mm});
            skLineSegment(sketch, "E28.6.23.0", {"start": v(14.53, -28.51) * mm, "end": v(13.69, -28.94) * mm});
            skLineSegment(sketch, "E28.9.23.0", {"start": v(13.69, -28.94) * mm, "end": v(12.45, -27.3) * mm});
            skLineSegment(sketch, "E28.2.24.0", {"start": v(19.57, -25.33) * mm, "end": v(18.67, -23.48) * mm});
            skLineSegment(sketch, "E28.3.24.0", {"start": v(18.8, -25.89) * mm, "end": v(19.57, -25.33) * mm});
            skLineSegment(sketch, "E28.6.24.0", {"start": v(18.8, -25.89) * mm, "end": v(18.05, -26.44) * mm});
            skLineSegment(sketch, "E28.9.24.0", {"start": v(18.05, -26.44) * mm, "end": v(16.57, -25.01) * mm});
            skLineSegment(sketch, "E28.2.25.0", {"start": v(23.3, -21.96) * mm, "end": v(22.11, -20.27) * mm});
            skLineSegment(sketch, "E28.3.25.0", {"start": v(22.63, -22.63) * mm, "end": v(23.3, -21.96) * mm});
            skLineSegment(sketch, "E28.6.25.0", {"start": v(22.63, -22.63) * mm, "end": v(21.96, -23.3) * mm});
            skLineSegment(sketch, "E28.9.25.0", {"start": v(21.96, -23.3) * mm, "end": v(20.27, -22.11) * mm});
            skLineSegment(sketch, "E28.2.26.0", {"start": v(26.44, -18.05) * mm, "end": v(25.01, -16.57) * mm});
            skLineSegment(sketch, "E28.3.26.0", {"start": v(25.89, -18.8) * mm, "end": v(26.44, -18.05) * mm});
            skLineSegment(sketch, "E28.6.26.0", {"start": v(25.89, -18.8) * mm, "end": v(25.33, -19.57) * mm});
            skLineSegment(sketch, "E28.9.26.0", {"start": v(25.33, -19.57) * mm, "end": v(23.48, -18.67) * mm});
            skLineSegment(sketch, "E28.2.27.0", {"start": v(28.94, -13.69) * mm, "end": v(27.3, -12.45) * mm});
            skLineSegment(sketch, "E28.3.27.0", {"start": v(28.51, -14.53) * mm, "end": v(28.94, -13.69) * mm});
            skLineSegment(sketch, "E28.6.27.0", {"start": v(28.51, -14.53) * mm, "end": v(28.08, -15.37) * mm});
            skLineSegment(sketch, "E28.9.27.0", {"start": v(28.08, -15.37) * mm, "end": v(26.11, -14.77) * mm});
            skLineSegment(sketch, "E28.2.28.0", {"start": v(30.73, -9) * mm, "end": v(28.9, -8.03) * mm});
            skLineSegment(sketch, "E28.3.28.0", {"start": v(30.43, -9.89) * mm, "end": v(30.73, -9) * mm});
            skLineSegment(sketch, "E28.6.28.0", {"start": v(30.43, -9.89) * mm, "end": v(30.14, -10.78) * mm});
            skLineSegment(sketch, "E28.9.28.0", {"start": v(30.14, -10.78) * mm, "end": v(28.1, -10.5) * mm});
            skLineSegment(sketch, "E28.2.29.0", {"start": v(31.75, -4.08) * mm, "end": v(29.8, -3.4) * mm});
            skLineSegment(sketch, "E28.3.29.0", {"start": v(31.6, -5) * mm, "end": v(31.75, -4.08) * mm});
            skLineSegment(sketch, "E28.6.29.0", {"start": v(31.6, -5) * mm, "end": v(31.46, -5.94) * mm});
            skLineSegment(sketch, "E28.9.29.0", {"start": v(31.46, -5.94) * mm, "end": v(29.4, -5.97) * mm});
            skLineSegment(sketch, "E28.2.30.0", {"start": v(32, 0.94) * mm, "end": v(29.97, 1.3) * mm});
            skLineSegment(sketch, "E28.3.30.0", {"start": v(32, 0) * mm, "end": v(32, 0.94) * mm});
            skLineSegment(sketch, "E28.6.30.0", {"start": v(32, 0) * mm, "end": v(32, -0.94) * mm});
            skLineSegment(sketch, "E28.9.30.0", {"start": v(32, -0.94) * mm, "end": v(29.97, -1.3) * mm});
            skLineSegment(sketch, "E28.2.31.0", {"start": v(31.46, 5.94) * mm, "end": v(29.4, 5.97) * mm});
            skLineSegment(sketch, "E28.3.31.0", {"start": v(31.6, 5) * mm, "end": v(31.46, 5.94) * mm});
            skLineSegment(sketch, "E28.6.31.0", {"start": v(31.6, 5) * mm, "end": v(31.75, 4.08) * mm});
            skLineSegment(sketch, "E28.9.31.0", {"start": v(31.75, 4.08) * mm, "end": v(29.8, 3.4) * mm});
            skLineSegment(sketch, "E28.2.32.0", {"start": v(30.14, 10.78) * mm, "end": v(28.1, 10.5) * mm});
            skLineSegment(sketch, "E28.3.32.0", {"start": v(30.43, 9.89) * mm, "end": v(30.14, 10.78) * mm});
            skLineSegment(sketch, "E28.6.32.0", {"start": v(30.43, 9.89) * mm, "end": v(30.73, 9) * mm});
            skLineSegment(sketch, "E28.9.32.0", {"start": v(30.73, 9) * mm, "end": v(28.9, 8.03) * mm});
            skLineSegment(sketch, "E28.2.33.0", {"start": v(28.08, 15.37) * mm, "end": v(26.11, 14.77) * mm});
            skLineSegment(sketch, "E28.3.33.0", {"start": v(28.51, 14.53) * mm, "end": v(28.08, 15.37) * mm});
            skLineSegment(sketch, "E28.6.33.0", {"start": v(28.51, 14.53) * mm, "end": v(28.94, 13.69) * mm});
            skLineSegment(sketch, "E28.9.33.0", {"start": v(28.94, 13.69) * mm, "end": v(27.3, 12.45) * mm});
            skLineSegment(sketch, "E28.2.34.0", {"start": v(25.33, 19.57) * mm, "end": v(23.48, 18.67) * mm});
            skLineSegment(sketch, "E28.3.34.0", {"start": v(25.89, 18.8) * mm, "end": v(25.33, 19.57) * mm});
            skLineSegment(sketch, "E28.6.34.0", {"start": v(25.89, 18.8) * mm, "end": v(26.44, 18.05) * mm});
            skLineSegment(sketch, "E28.9.34.0", {"start": v(26.44, 18.05) * mm, "end": v(25.01, 16.57) * mm});
            skLineSegment(sketch, "E28.2.35.0", {"start": v(21.96, 23.3) * mm, "end": v(20.27, 22.11) * mm});
            skLineSegment(sketch, "E28.3.35.0", {"start": v(22.63, 22.63) * mm, "end": v(21.96, 23.3) * mm});
            skLineSegment(sketch, "E28.6.35.0", {"start": v(22.63, 22.63) * mm, "end": v(23.3, 21.96) * mm});
            skLineSegment(sketch, "E28.9.35.0", {"start": v(23.3, 21.96) * mm, "end": v(22.11, 20.27) * mm});
            skLineSegment(sketch, "E28.2.36.0", {"start": v(18.05, 26.44) * mm, "end": v(16.57, 25.01) * mm});
            skLineSegment(sketch, "E28.3.36.0", {"start": v(18.8, 25.89) * mm, "end": v(18.05, 26.44) * mm});
            skLineSegment(sketch, "E28.6.36.0", {"start": v(18.8, 25.89) * mm, "end": v(19.57, 25.33) * mm});
            skLineSegment(sketch, "E28.9.36.0", {"start": v(19.57, 25.33) * mm, "end": v(18.67, 23.48) * mm});
            skLineSegment(sketch, "E28.2.37.0", {"start": v(13.69, 28.94) * mm, "end": v(12.45, 27.3) * mm});
            skLineSegment(sketch, "E28.3.37.0", {"start": v(14.53, 28.51) * mm, "end": v(13.69, 28.94) * mm});
            skLineSegment(sketch, "E28.6.37.0", {"start": v(14.53, 28.51) * mm, "end": v(15.37, 28.08) * mm});
            skLineSegment(sketch, "E28.9.37.0", {"start": v(15.37, 28.08) * mm, "end": v(14.77, 26.11) * mm});
            skLineSegment(sketch, "E28.2.38.0", {"start": v(9, 30.73) * mm, "end": v(8.03, 28.9) * mm});
            skLineSegment(sketch, "E28.3.38.0", {"start": v(9.89, 30.43) * mm, "end": v(9, 30.73) * mm});
            skLineSegment(sketch, "E28.6.38.0", {"start": v(9.89, 30.43) * mm, "end": v(10.78, 30.14) * mm});
            skLineSegment(sketch, "E28.9.38.0", {"start": v(10.78, 30.14) * mm, "end": v(10.5, 28.1) * mm});
            skLineSegment(sketch, "E28.2.39.0", {"start": v(4.08, 31.75) * mm, "end": v(3.4, 29.8) * mm});
            skLineSegment(sketch, "E28.3.39.0", {"start": v(5, 31.6) * mm, "end": v(4.08, 31.75) * mm});
            skLineSegment(sketch, "E28.6.39.0", {"start": v(5, 31.6) * mm, "end": v(5.94, 31.46) * mm});
            skLineSegment(sketch, "E28.9.39.0", {"start": v(5.94, 31.46) * mm, "end": v(5.97, 29.4) * mm});
            skSolve(sketch);
        }
        {
            var Q0;
            Q0 = qSketchRegion(id + "F14", true);
            extrude(context, id + "F15", {"entities" : qUnion([Q0]), "operationType" : NewBodyOperationType.ADD, "depth" : 4 * mm, "offsetDistance" : 25 * mm});
        }
        {
            var Q0;
            Q0=makeQuery(id+"F7.opExtrude","CAP_FACE",FACE,{"disambiguationData":[OSD([sQuery(id+"F0.wireOp",EDGE,"E0")])],"isStart":false});
            var sketch = newSketch(context, id + "F16", { "sketchPlane" : qUnion([Q0])});
            skCircle(sketch, "E29", {"center": v(40, 0) * mm, "radius": 7.5 * mm});
            skLineSegment(sketch, "E30", {"start": v(40, 0) * mm, "end": v(40, 7.5) * mm, "construction": true});
            skLineSegment(sketch, "E31", {"start": v(38.68, 7.38) * mm, "end": v(39.06, 9.5) * mm});
            skLineSegment(sketch, "E32", {"start": v(39.06, 9.5) * mm, "end": v(40.94, 9.5) * mm});
            skLineSegment(sketch, "E33.MirrorCS", {"start": v(41.32, 7.38) * mm, "end": v(40.94, 9.5) * mm});
            skLineSegment(sketch, "E34.1.0", {"start": v(34.6, 5.2) * mm, "end": v(33.65, 7.13) * mm});
            skLineSegment(sketch, "E34.1.1", {"start": v(33.65, 7.13) * mm, "end": v(35.18, 8.24) * mm});
            skLineSegment(sketch, "E34.1.2", {"start": v(36.72, 6.75) * mm, "end": v(35.18, 8.24) * mm});
            skLineSegment(sketch, "E34.2.0", {"start": v(32.57, 1.03) * mm, "end": v(30.67, 2.04) * mm});
            skLineSegment(sketch, "E34.2.1", {"start": v(30.67, 2.04) * mm, "end": v(31.26, 3.83) * mm});
            skLineSegment(sketch, "E34.2.2", {"start": v(33.38, 3.53) * mm, "end": v(31.26, 3.83) * mm});
            skLineSegment(sketch, "E35.1.3.0", {"start": v(33.38, -3.53) * mm, "end": v(31.26, -3.83) * mm});
            skLineSegment(sketch, "E35.3.3.0", {"start": v(31.26, -3.83) * mm, "end": v(30.67, -2.04) * mm});
            skLineSegment(sketch, "E35.6.3.0", {"start": v(32.57, -1.03) * mm, "end": v(30.67, -2.04) * mm});
            skLineSegment(sketch, "E35.1.4.0", {"start": v(36.72, -6.75) * mm, "end": v(35.18, -8.24) * mm});
            skLineSegment(sketch, "E35.3.4.0", {"start": v(35.18, -8.24) * mm, "end": v(33.65, -7.13) * mm});
            skLineSegment(sketch, "E35.6.4.0", {"start": v(34.6, -5.2) * mm, "end": v(33.65, -7.13) * mm});
            skLineSegment(sketch, "E35.1.5.0", {"start": v(41.32, -7.38) * mm, "end": v(40.94, -9.5) * mm});
            skLineSegment(sketch, "E35.3.5.0", {"start": v(40.94, -9.5) * mm, "end": v(39.06, -9.5) * mm});
            skLineSegment(sketch, "E35.6.5.0", {"start": v(38.68, -7.38) * mm, "end": v(39.06, -9.5) * mm});
            skLineSegment(sketch, "E35.1.6.0", {"start": v(45.4, -5.2) * mm, "end": v(46.35, -7.13) * mm});
            skLineSegment(sketch, "E35.3.6.0", {"start": v(46.35, -7.13) * mm, "end": v(44.82, -8.24) * mm});
            skLineSegment(sketch, "E35.6.6.0", {"start": v(43.28, -6.75) * mm, "end": v(44.82, -8.24) * mm});
            skLineSegment(sketch, "E35.1.7.0", {"start": v(47.43, -1.03) * mm, "end": v(49.33, -2.04) * mm});
            skLineSegment(sketch, "E35.3.7.0", {"start": v(49.33, -2.04) * mm, "end": v(48.74, -3.83) * mm});
            skLineSegment(sketch, "E35.6.7.0", {"start": v(46.62, -3.53) * mm, "end": v(48.74, -3.83) * mm});
            skLineSegment(sketch, "E35.1.8.0", {"start": v(46.62, 3.53) * mm, "end": v(48.74, 3.83) * mm});
            skLineSegment(sketch, "E35.3.8.0", {"start": v(48.74, 3.83) * mm, "end": v(49.33, 2.04) * mm});
            skLineSegment(sketch, "E35.6.8.0", {"start": v(47.43, 1.03) * mm, "end": v(49.33, 2.04) * mm});
            skLineSegment(sketch, "E35.1.9.0", {"start": v(43.28, 6.75) * mm, "end": v(44.82, 8.24) * mm});
            skLineSegment(sketch, "E35.3.9.0", {"start": v(44.82, 8.24) * mm, "end": v(46.35, 7.13) * mm});
            skLineSegment(sketch, "E35.6.9.0", {"start": v(45.4, 5.2) * mm, "end": v(46.35, 7.13) * mm});
            skSolve(sketch);
        }
        {
            var Q0;
            Q0 = qSketchRegion(id + "F16", true);
            extrude(context, id + "F17", {"entities" : qUnion([Q0]), "operationType" : NewBodyOperationType.ADD, "depth" : 4 * mm, "offsetDistance" : 25 * mm});
        }
        {
            var Q0;
            Q0=makeQuery(id+"F17.opExtrude","CAP_FACE",FACE,{"disambiguationData":[OSD([sQuery(id+"F16.wireOp",EDGE,"E29"),sQuery(id+"F16.wireOp",EDGE,"E31"),sQuery(id+"F16.wireOp",EDGE,"E32"),sQuery(id+"F16.wireOp",EDGE,"E33.MirrorCS"),sQuery(id+"F16.wireOp",EDGE,"E34.1.0"),sQuery(id+"F16.wireOp",EDGE,"E34.1.1"),sQuery(id+"F16.wireOp",EDGE,"E34.1.2"),sQuery(id+"F16.wireOp",EDGE,"E34.2.0"),sQuery(id+"F16.wireOp",EDGE,"E34.2.1"),sQuery(id+"F16.wireOp",EDGE,"E34.2.2"),sQuery(id+"F16.wireOp",EDGE,"E35.1.3.0"),sQuery(id+"F16.wireOp",EDGE,"E35.3.3.0"),sQuery(id+"F16.wireOp",EDGE,"E35.6.3.0"),sQuery(id+"F16.wireOp",EDGE,"E35.1.4.0"),sQuery(id+"F16.wireOp",EDGE,"E35.3.4.0"),sQuery(id+"F16.wireOp",EDGE,"E35.6.4.0"),sQuery(id+"F16.wireOp",EDGE,"E35.1.5.0"),sQuery(id+"F16.wireOp",EDGE,"E35.3.5.0"),sQuery(id+"F16.wireOp",EDGE,"E35.6.5.0"),sQuery(id+"F16.wireOp",EDGE,"E35.1.6.0"),sQuery(id+"F16.wireOp",EDGE,"E35.3.6.0"),sQuery(id+"F16.wireOp",EDGE,"E35.6.6.0"),sQuery(id+"F16.wireOp",EDGE,"E35.1.7.0"),sQuery(id+"F16.wireOp",EDGE,"E35.3.7.0"),sQuery(id+"F16.wireOp",EDGE,"E35.6.7.0"),sQuery(id+"F16.wireOp",EDGE,"E35.1.8.0"),sQuery(id+"F16.wireOp",EDGE,"E35.3.8.0"),sQuery(id+"F16.wireOp",EDGE,"E35.6.8.0"),sQuery(id+"F16.wireOp",EDGE,"E35.1.9.0"),sQuery(id+"F16.wireOp",EDGE,"E35.3.9.0"),sQuery(id+"F16.wireOp",EDGE,"E35.6.9.0")])],"isStart":false});
            var sketch = newSketch(context, id + "F18", { "sketchPlane" : qUnion([Q0])});
            skCircle(sketch, "E36.0", {"center": v(40, 0) * mm, "radius": 3 * mm});
            skSolve(sketch);
        }
        {
            var Q0;
            Q0 = qSketchRegion(id + "F18", true);
            extrude(context, id + "F19", {"entities" : qUnion([Q0]), "operationType" : NewBodyOperationType.ADD, "depth" : 2 * mm, "offsetDistance" : 25 * mm});
        }
        {
            var Q0;
            Q0=makeQuery(id+"F19.opExtrude","CAP_FACE",FACE,{"disambiguationData":[OSD([sQuery(id+"F18.wireOp",EDGE,"E36.0")])],"isStart":false});
            var sketch = newSketch(context, id + "F20", { "sketchPlane" : qUnion([Q0])});
            skCircle(sketch, "E37", {"center": v(0, 0) * mm, "radius": 98 * mm});
            skCircle(sketch, "E38.0", {"center": v(0, 0) * mm, "radius": 5 * mm});
            skSolve(sketch);
        }
        {
            var Q0;
            Q0 = qSketchRegion(id + "F20", true);
            extrude(context, id + "F21", {"entities" : qUnion([Q0]), "depth" : 1 * mm, "offsetDistance" : 25 * mm});
        }
        {
            var Q0;
            Q0=makeQuery(id+"F21.opExtrude","SWEPT_BODY",BODY,{"disambiguationData":[OSD([sQuery(id+"F20.wireOp",EDGE,"E37"),sQuery(id+"F20.wireOp",EDGE,"E38.0")])]});
            var Q1;
            Q1=makeQuery(id+"F1.opExtrude","SWEPT_BODY",BODY,{"disambiguationData":[OSD([sQuery(id+"F0.wireOp",EDGE,"E0")])]});
            booleanBodies(context, id + "F22", {"operationType" : BooleanOperationType.SUBTRACTION, "tools" : qUnion([Q0]), "targets" : qUnion([Q1]), "keepTools" : true});
        }
        {
            var Q0;
            Q0=makeQuery(id+"F21.opExtrude","CAP_FACE",FACE,{"disambiguationData":[OSD([sQuery(id+"F20.wireOp",EDGE,"E37"),sQuery(id+"F20.wireOp",EDGE,"E38.0")])],"isStart":true});
            var sketch = newSketch(context, id + "F23", { "sketchPlane" : qUnion([Q0])});
            skCircle(sketch, "E39.0", {"center": v(-40, 0) * mm, "radius": 3 * mm});
            skCircle(sketch, "E40", {"center": v(-40, 0) * mm, "radius": 5 * mm});
            skSolve(sketch);
        }
        {
            var Q0;
            Q0 = qSketchRegion(id + "F23", true);
            extrude(context, id + "F24", {"entities" : qUnion([Q0]), "operationType" : NewBodyOperationType.ADD, "endBound" : BoundingType.UP_TO_NEXT, "depth" : 25 * mm, "offsetDistance" : 25 * mm});
        }
        {
            var Q0;
            Q0=makeQuery(id+"F21.opExtrude","CAP_FACE",FACE,{"disambiguationData":[OSD([sQuery(id+"F20.wireOp",EDGE,"E37"),sQuery(id+"F20.wireOp",EDGE,"E38.0")])],"isStart":false});
            var sketch = newSketch(context, id + "F25", { "sketchPlane" : qUnion([Q0])});
            skLineSegment(sketch, "E41.bottom", {"start": v(1.5, 71) * mm, "end": v(-1.5, 71) * mm});
            skLineSegment(sketch, "E41.top", {"start": v(1.5, 91) * mm, "end": v(-1.5, 91) * mm});
            skLineSegment(sketch, "E41.left", {"start": v(1.5, 71) * mm, "end": v(1.5, 91) * mm});
            skLineSegment(sketch, "E41.right", {"start": v(-1.5, 71) * mm, "end": v(-1.5, 91) * mm});
            skPoint(sketch, "E41.middle", {"position": v(0, 81) * mm});
            skLineSegment(sketch, "E42.1.0", {"start": v(-36.8, 60.74) * mm, "end": v(-46.8, 78.06) * mm});
            skLineSegment(sketch, "E42.1.1", {"start": v(-44.2, 79.56) * mm, "end": v(-46.8, 78.06) * mm});
            skLineSegment(sketch, "E42.1.2", {"start": v(-34.2, 62.24) * mm, "end": v(-44.2, 79.56) * mm});
            skLineSegment(sketch, "E42.1.3", {"start": v(-34.2, 62.24) * mm, "end": v(-36.8, 60.74) * mm});
            skLineSegment(sketch, "E42.2.0", {"start": v(-62.24, 34.2) * mm, "end": v(-79.56, 44.2) * mm});
            skLineSegment(sketch, "E42.2.1", {"start": v(-78.06, 46.8) * mm, "end": v(-79.56, 44.2) * mm});
            skLineSegment(sketch, "E42.2.2", {"start": v(-60.74, 36.8) * mm, "end": v(-78.06, 46.8) * mm});
            skLineSegment(sketch, "E42.2.3", {"start": v(-60.74, 36.8) * mm, "end": v(-62.24, 34.2) * mm});
            skPoint(sketch, "E42.center", {"position": v(0, 0) * mm});
            skLineSegment(sketch, "E43.1.3.0", {"start": v(-71, -1.5) * mm, "end": v(-91, -1.5) * mm});
            skLineSegment(sketch, "E43.3.3.0", {"start": v(-91, 1.5) * mm, "end": v(-91, -1.5) * mm});
            skLineSegment(sketch, "E43.6.3.0", {"start": v(-71, 1.5) * mm, "end": v(-91, 1.5) * mm});
            skLineSegment(sketch, "E43.9.3.0", {"start": v(-71, 1.5) * mm, "end": v(-71, -1.5) * mm});
            skLineSegment(sketch, "E43.1.4.0", {"start": v(-60.74, -36.8) * mm, "end": v(-78.06, -46.8) * mm});
            skLineSegment(sketch, "E43.3.4.0", {"start": v(-79.56, -44.2) * mm, "end": v(-78.06, -46.8) * mm});
            skLineSegment(sketch, "E43.6.4.0", {"start": v(-62.24, -34.2) * mm, "end": v(-79.56, -44.2) * mm});
            skLineSegment(sketch, "E43.9.4.0", {"start": v(-62.24, -34.2) * mm, "end": v(-60.74, -36.8) * mm});
            skLineSegment(sketch, "E43.1.5.0", {"start": v(-34.2, -62.24) * mm, "end": v(-44.2, -79.56) * mm});
            skLineSegment(sketch, "E43.3.5.0", {"start": v(-46.8, -78.06) * mm, "end": v(-44.2, -79.56) * mm});
            skLineSegment(sketch, "E43.6.5.0", {"start": v(-36.8, -60.74) * mm, "end": v(-46.8, -78.06) * mm});
            skLineSegment(sketch, "E43.9.5.0", {"start": v(-36.8, -60.74) * mm, "end": v(-34.2, -62.24) * mm});
            skLineSegment(sketch, "E43.1.6.0", {"start": v(1.5, -71) * mm, "end": v(1.5, -91) * mm});
            skLineSegment(sketch, "E43.3.6.0", {"start": v(-1.5, -91) * mm, "end": v(1.5, -91) * mm});
            skLineSegment(sketch, "E43.6.6.0", {"start": v(-1.5, -71) * mm, "end": v(-1.5, -91) * mm});
            skLineSegment(sketch, "E43.9.6.0", {"start": v(-1.5, -71) * mm, "end": v(1.5, -71) * mm});
            skLineSegment(sketch, "E43.1.7.0", {"start": v(36.8, -60.74) * mm, "end": v(46.8, -78.06) * mm});
            skLineSegment(sketch, "E43.3.7.0", {"start": v(44.2, -79.56) * mm, "end": v(46.8, -78.06) * mm});
            skLineSegment(sketch, "E43.6.7.0", {"start": v(34.2, -62.24) * mm, "end": v(44.2, -79.56) * mm});
            skLineSegment(sketch, "E43.9.7.0", {"start": v(34.2, -62.24) * mm, "end": v(36.8, -60.74) * mm});
            skLineSegment(sketch, "E43.1.8.0", {"start": v(62.24, -34.2) * mm, "end": v(79.56, -44.2) * mm});
            skLineSegment(sketch, "E43.3.8.0", {"start": v(78.06, -46.8) * mm, "end": v(79.56, -44.2) * mm});
            skLineSegment(sketch, "E43.6.8.0", {"start": v(60.74, -36.8) * mm, "end": v(78.06, -46.8) * mm});
            skLineSegment(sketch, "E43.9.8.0", {"start": v(60.74, -36.8) * mm, "end": v(62.24, -34.2) * mm});
            skLineSegment(sketch, "E43.1.9.0", {"start": v(71, 1.5) * mm, "end": v(91, 1.5) * mm});
            skLineSegment(sketch, "E43.3.9.0", {"start": v(91, -1.5) * mm, "end": v(91, 1.5) * mm});
            skLineSegment(sketch, "E43.6.9.0", {"start": v(71, -1.5) * mm, "end": v(91, -1.5) * mm});
            skLineSegment(sketch, "E43.9.9.0", {"start": v(71, -1.5) * mm, "end": v(71, 1.5) * mm});
            skLineSegment(sketch, "E43.1.10.0", {"start": v(60.74, 36.8) * mm, "end": v(78.06, 46.8) * mm});
            skLineSegment(sketch, "E43.3.10.0", {"start": v(79.56, 44.2) * mm, "end": v(78.06, 46.8) * mm});
            skLineSegment(sketch, "E43.6.10.0", {"start": v(62.24, 34.2) * mm, "end": v(79.56, 44.2) * mm});
            skLineSegment(sketch, "E43.9.10.0", {"start": v(62.24, 34.2) * mm, "end": v(60.74, 36.8) * mm});
            skLineSegment(sketch, "E43.1.11.0", {"start": v(34.2, 62.24) * mm, "end": v(44.2, 79.56) * mm});
            skLineSegment(sketch, "E43.3.11.0", {"start": v(46.8, 78.06) * mm, "end": v(44.2, 79.56) * mm});
            skLineSegment(sketch, "E43.6.11.0", {"start": v(36.8, 60.74) * mm, "end": v(46.8, 78.06) * mm});
            skLineSegment(sketch, "E43.9.11.0", {"start": v(36.8, 60.74) * mm, "end": v(34.2, 62.24) * mm});
            skSolve(sketch);
        }
        {
            var Q0;
            Q0 = qSketchRegion(id + "F25", true);
            extrude(context, id + "F26", {"entities" : qUnion([Q0]), "operationType" : NewBodyOperationType.REMOVE, "oppositeDirection" : true, "depth" : 0.5 * mm, "offsetDistance" : 25 * mm});
        }
        {
            var Q0;
            Q0=makeQuery(id+"F21.opExtrude","CAP_FACE",FACE,{"disambiguationData":[OSD([sQuery(id+"F20.wireOp",EDGE,"E37"),sQuery(id+"F20.wireOp",EDGE,"E38.0")])],"isStart":false});
            var sketch = newSketch(context, id + "F27", { "sketchPlane" : qUnion([Q0])});
            skLineSegment(sketch, "E44.bottom", {"start": v(0.75, 78.5) * mm, "end": v(-0.75, 78.5) * mm});
            skLineSegment(sketch, "E44.top", {"start": v(0.75, 90.5) * mm, "end": v(-0.75, 90.5) * mm});
            skLineSegment(sketch, "E44.left", {"start": v(0.75, 78.5) * mm, "end": v(0.75, 90.5) * mm});
            skLineSegment(sketch, "E44.right", {"start": v(-0.75, 78.5) * mm, "end": v(-0.75, 90.5) * mm});
            skPoint(sketch, "E44.middle", {"position": v(0, 84.5) * mm});
            skLineSegment(sketch, "E45.1.0", {"start": v(-8.71, 90.08) * mm, "end": v(-10.2, 89.93) * mm});
            skLineSegment(sketch, "E45.1.1", {"start": v(-8.95, 78) * mm, "end": v(-10.2, 89.93) * mm});
            skLineSegment(sketch, "E45.1.2", {"start": v(-7.46, 78.15) * mm, "end": v(-8.71, 90.08) * mm});
            skLineSegment(sketch, "E45.1.3", {"start": v(-7.46, 78.15) * mm, "end": v(-8.95, 78) * mm});
            skLineSegment(sketch, "E45.2.0", {"start": v(-18.08, 88.68) * mm, "end": v(-19.55, 88.37) * mm});
            skLineSegment(sketch, "E45.2.1", {"start": v(-17.05, 76.63) * mm, "end": v(-19.55, 88.37) * mm});
            skLineSegment(sketch, "E45.2.2", {"start": v(-15.59, 76.94) * mm, "end": v(-18.08, 88.68) * mm});
            skLineSegment(sketch, "E45.2.3", {"start": v(-15.59, 76.94) * mm, "end": v(-17.05, 76.63) * mm});
            skPoint(sketch, "E45.center", {"position": v(0, 0) * mm});
            skLineSegment(sketch, "E46.2.3.0", {"start": v(-27.25, 86.3) * mm, "end": v(-28.68, 85.84) * mm});
            skLineSegment(sketch, "E46.3.3.0", {"start": v(-24.97, 74.43) * mm, "end": v(-28.68, 85.84) * mm});
            skLineSegment(sketch, "E46.6.3.0", {"start": v(-23.54, 74.89) * mm, "end": v(-27.25, 86.3) * mm});
            skLineSegment(sketch, "E46.9.3.0", {"start": v(-23.54, 74.89) * mm, "end": v(-24.97, 74.43) * mm});
            skLineSegment(sketch, "E46.2.4.0", {"start": v(-36.12, 82.98) * mm, "end": v(-37.5, 82.37) * mm});
            skLineSegment(sketch, "E46.3.4.0", {"start": v(-32.61, 71.4) * mm, "end": v(-37.5, 82.37) * mm});
            skLineSegment(sketch, "E46.6.4.0", {"start": v(-31.24, 72.02) * mm, "end": v(-36.12, 82.98) * mm});
            skLineSegment(sketch, "E46.9.4.0", {"start": v(-31.24, 72.02) * mm, "end": v(-32.61, 71.4) * mm});
            skLineSegment(sketch, "E46.2.5.0", {"start": v(-44.6, 78.75) * mm, "end": v(-45.9, 78) * mm});
            skLineSegment(sketch, "E46.3.5.0", {"start": v(-39.9, 67.6) * mm, "end": v(-45.9, 78) * mm});
            skLineSegment(sketch, "E46.6.5.0", {"start": v(-38.6, 68.36) * mm, "end": v(-44.6, 78.75) * mm});
            skLineSegment(sketch, "E46.9.5.0", {"start": v(-38.6, 68.36) * mm, "end": v(-39.9, 67.6) * mm});
            skLineSegment(sketch, "E46.2.6.0", {"start": v(-52.59, 73.66) * mm, "end": v(-53.8, 72.78) * mm});
            skLineSegment(sketch, "E46.3.6.0", {"start": v(-46.75, 63.07) * mm, "end": v(-53.8, 72.78) * mm});
            skLineSegment(sketch, "E46.6.6.0", {"start": v(-45.53, 63.95) * mm, "end": v(-52.59, 73.66) * mm});
            skLineSegment(sketch, "E46.9.6.0", {"start": v(-45.53, 63.95) * mm, "end": v(-46.75, 63.07) * mm});
            skLineSegment(sketch, "E46.2.7.0", {"start": v(-60, 67.76) * mm, "end": v(-61.11, 66.75) * mm});
            skLineSegment(sketch, "E46.3.7.0", {"start": v(-53.08, 57.84) * mm, "end": v(-61.11, 66.75) * mm});
            skLineSegment(sketch, "E46.6.7.0", {"start": v(-51.97, 58.84) * mm, "end": v(-60, 67.76) * mm});
            skLineSegment(sketch, "E46.9.7.0", {"start": v(-51.97, 58.84) * mm, "end": v(-53.08, 57.84) * mm});
            skLineSegment(sketch, "E46.2.8.0", {"start": v(-66.75, 61.11) * mm, "end": v(-67.76, 60) * mm});
            skLineSegment(sketch, "E46.3.8.0", {"start": v(-58.84, 51.97) * mm, "end": v(-67.76, 60) * mm});
            skLineSegment(sketch, "E46.6.8.0", {"start": v(-57.84, 53.08) * mm, "end": v(-66.75, 61.11) * mm});
            skLineSegment(sketch, "E46.9.8.0", {"start": v(-57.84, 53.08) * mm, "end": v(-58.84, 51.97) * mm});
            skLineSegment(sketch, "E46.2.9.0", {"start": v(-72.78, 53.8) * mm, "end": v(-73.66, 52.59) * mm});
            skLineSegment(sketch, "E46.3.9.0", {"start": v(-63.95, 45.53) * mm, "end": v(-73.66, 52.59) * mm});
            skLineSegment(sketch, "E46.6.9.0", {"start": v(-63.07, 46.75) * mm, "end": v(-72.78, 53.8) * mm});
            skLineSegment(sketch, "E46.9.9.0", {"start": v(-63.07, 46.75) * mm, "end": v(-63.95, 45.53) * mm});
            skLineSegment(sketch, "E46.2.10.0", {"start": v(-78, 45.9) * mm, "end": v(-78.75, 44.6) * mm});
            skLineSegment(sketch, "E46.3.10.0", {"start": v(-68.36, 38.6) * mm, "end": v(-78.75, 44.6) * mm});
            skLineSegment(sketch, "E46.6.10.0", {"start": v(-67.6, 39.9) * mm, "end": v(-78, 45.9) * mm});
            skLineSegment(sketch, "E46.9.10.0", {"start": v(-67.6, 39.9) * mm, "end": v(-68.36, 38.6) * mm});
            skLineSegment(sketch, "E46.2.11.0", {"start": v(-82.37, 37.5) * mm, "end": v(-82.98, 36.12) * mm});
            skLineSegment(sketch, "E46.3.11.0", {"start": v(-72.02, 31.24) * mm, "end": v(-82.98, 36.12) * mm});
            skLineSegment(sketch, "E46.6.11.0", {"start": v(-71.4, 32.61) * mm, "end": v(-82.37, 37.5) * mm});
            skLineSegment(sketch, "E46.9.11.0", {"start": v(-71.4, 32.61) * mm, "end": v(-72.02, 31.24) * mm});
            skLineSegment(sketch, "E46.2.12.0", {"start": v(-85.84, 28.68) * mm, "end": v(-86.3, 27.25) * mm});
            skLineSegment(sketch, "E46.3.12.0", {"start": v(-74.89, 23.54) * mm, "end": v(-86.3, 27.25) * mm});
            skLineSegment(sketch, "E46.6.12.0", {"start": v(-74.43, 24.97) * mm, "end": v(-85.84, 28.68) * mm});
            skLineSegment(sketch, "E46.9.12.0", {"start": v(-74.43, 24.97) * mm, "end": v(-74.89, 23.54) * mm});
            skLineSegment(sketch, "E46.2.13.0", {"start": v(-88.37, 19.55) * mm, "end": v(-88.68, 18.08) * mm});
            skLineSegment(sketch, "E46.3.13.0", {"start": v(-76.94, 15.59) * mm, "end": v(-88.68, 18.08) * mm});
            skLineSegment(sketch, "E46.6.13.0", {"start": v(-76.63, 17.05) * mm, "end": v(-88.37, 19.55) * mm});
            skLineSegment(sketch, "E46.9.13.0", {"start": v(-76.63, 17.05) * mm, "end": v(-76.94, 15.59) * mm});
            skLineSegment(sketch, "E46.2.14.0", {"start": v(-89.93, 10.2) * mm, "end": v(-90.08, 8.71) * mm});
            skLineSegment(sketch, "E46.3.14.0", {"start": v(-78.15, 7.46) * mm, "end": v(-90.08, 8.71) * mm});
            skLineSegment(sketch, "E46.6.14.0", {"start": v(-78, 8.95) * mm, "end": v(-89.93, 10.2) * mm});
            skLineSegment(sketch, "E46.9.14.0", {"start": v(-78, 8.95) * mm, "end": v(-78.15, 7.46) * mm});
            skLineSegment(sketch, "E46.2.15.0", {"start": v(-90.5, 0.75) * mm, "end": v(-90.5, -0.75) * mm});
            skLineSegment(sketch, "E46.3.15.0", {"start": v(-78.5, -0.75) * mm, "end": v(-90.5, -0.75) * mm});
            skLineSegment(sketch, "E46.6.15.0", {"start": v(-78.5, 0.75) * mm, "end": v(-90.5, 0.75) * mm});
            skLineSegment(sketch, "E46.9.15.0", {"start": v(-78.5, 0.75) * mm, "end": v(-78.5, -0.75) * mm});
            skLineSegment(sketch, "E46.2.16.0", {"start": v(-90.08, -8.71) * mm, "end": v(-89.93, -10.2) * mm});
            skLineSegment(sketch, "E46.3.16.0", {"start": v(-78, -8.95) * mm, "end": v(-89.93, -10.2) * mm});
            skLineSegment(sketch, "E46.6.16.0", {"start": v(-78.15, -7.46) * mm, "end": v(-90.08, -8.71) * mm});
            skLineSegment(sketch, "E46.9.16.0", {"start": v(-78.15, -7.46) * mm, "end": v(-78, -8.95) * mm});
            skLineSegment(sketch, "E46.2.17.0", {"start": v(-88.68, -18.08) * mm, "end": v(-88.37, -19.55) * mm});
            skLineSegment(sketch, "E46.3.17.0", {"start": v(-76.63, -17.05) * mm, "end": v(-88.37, -19.55) * mm});
            skLineSegment(sketch, "E46.6.17.0", {"start": v(-76.94, -15.59) * mm, "end": v(-88.68, -18.08) * mm});
            skLineSegment(sketch, "E46.9.17.0", {"start": v(-76.94, -15.59) * mm, "end": v(-76.63, -17.05) * mm});
            skLineSegment(sketch, "E46.2.18.0", {"start": v(-86.3, -27.25) * mm, "end": v(-85.84, -28.68) * mm});
            skLineSegment(sketch, "E46.3.18.0", {"start": v(-74.43, -24.97) * mm, "end": v(-85.84, -28.68) * mm});
            skLineSegment(sketch, "E46.6.18.0", {"start": v(-74.89, -23.54) * mm, "end": v(-86.3, -27.25) * mm});
            skLineSegment(sketch, "E46.9.18.0", {"start": v(-74.89, -23.54) * mm, "end": v(-74.43, -24.97) * mm});
            skLineSegment(sketch, "E46.2.19.0", {"start": v(-82.98, -36.12) * mm, "end": v(-82.37, -37.5) * mm});
            skLineSegment(sketch, "E46.3.19.0", {"start": v(-71.4, -32.61) * mm, "end": v(-82.37, -37.5) * mm});
            skLineSegment(sketch, "E46.6.19.0", {"start": v(-72.02, -31.24) * mm, "end": v(-82.98, -36.12) * mm});
            skLineSegment(sketch, "E46.9.19.0", {"start": v(-72.02, -31.24) * mm, "end": v(-71.4, -32.61) * mm});
            skLineSegment(sketch, "E46.2.20.0", {"start": v(-78.75, -44.6) * mm, "end": v(-78, -45.9) * mm});
            skLineSegment(sketch, "E46.3.20.0", {"start": v(-67.6, -39.9) * mm, "end": v(-78, -45.9) * mm});
            skLineSegment(sketch, "E46.6.20.0", {"start": v(-68.36, -38.6) * mm, "end": v(-78.75, -44.6) * mm});
            skLineSegment(sketch, "E46.9.20.0", {"start": v(-68.36, -38.6) * mm, "end": v(-67.6, -39.9) * mm});
            skLineSegment(sketch, "E46.2.21.0", {"start": v(-73.66, -52.59) * mm, "end": v(-72.78, -53.8) * mm});
            skLineSegment(sketch, "E46.3.21.0", {"start": v(-63.07, -46.75) * mm, "end": v(-72.78, -53.8) * mm});
            skLineSegment(sketch, "E46.6.21.0", {"start": v(-63.95, -45.53) * mm, "end": v(-73.66, -52.59) * mm});
            skLineSegment(sketch, "E46.9.21.0", {"start": v(-63.95, -45.53) * mm, "end": v(-63.07, -46.75) * mm});
            skLineSegment(sketch, "E46.2.22.0", {"start": v(-67.76, -60) * mm, "end": v(-66.75, -61.11) * mm});
            skLineSegment(sketch, "E46.3.22.0", {"start": v(-57.84, -53.08) * mm, "end": v(-66.75, -61.11) * mm});
            skLineSegment(sketch, "E46.6.22.0", {"start": v(-58.84, -51.97) * mm, "end": v(-67.76, -60) * mm});
            skLineSegment(sketch, "E46.9.22.0", {"start": v(-58.84, -51.97) * mm, "end": v(-57.84, -53.08) * mm});
            skLineSegment(sketch, "E46.2.23.0", {"start": v(-61.11, -66.75) * mm, "end": v(-60, -67.76) * mm});
            skLineSegment(sketch, "E46.3.23.0", {"start": v(-51.97, -58.84) * mm, "end": v(-60, -67.76) * mm});
            skLineSegment(sketch, "E46.6.23.0", {"start": v(-53.08, -57.84) * mm, "end": v(-61.11, -66.75) * mm});
            skLineSegment(sketch, "E46.9.23.0", {"start": v(-53.08, -57.84) * mm, "end": v(-51.97, -58.84) * mm});
            skLineSegment(sketch, "E46.2.24.0", {"start": v(-53.8, -72.78) * mm, "end": v(-52.59, -73.66) * mm});
            skLineSegment(sketch, "E46.3.24.0", {"start": v(-45.53, -63.95) * mm, "end": v(-52.59, -73.66) * mm});
            skLineSegment(sketch, "E46.6.24.0", {"start": v(-46.75, -63.07) * mm, "end": v(-53.8, -72.78) * mm});
            skLineSegment(sketch, "E46.9.24.0", {"start": v(-46.75, -63.07) * mm, "end": v(-45.53, -63.95) * mm});
            skLineSegment(sketch, "E46.2.25.0", {"start": v(-45.9, -78) * mm, "end": v(-44.6, -78.75) * mm});
            skLineSegment(sketch, "E46.3.25.0", {"start": v(-38.6, -68.36) * mm, "end": v(-44.6, -78.75) * mm});
            skLineSegment(sketch, "E46.6.25.0", {"start": v(-39.9, -67.6) * mm, "end": v(-45.9, -78) * mm});
            skLineSegment(sketch, "E46.9.25.0", {"start": v(-39.9, -67.6) * mm, "end": v(-38.6, -68.36) * mm});
            skLineSegment(sketch, "E46.2.26.0", {"start": v(-37.5, -82.37) * mm, "end": v(-36.12, -82.98) * mm});
            skLineSegment(sketch, "E46.3.26.0", {"start": v(-31.24, -72.02) * mm, "end": v(-36.12, -82.98) * mm});
            skLineSegment(sketch, "E46.6.26.0", {"start": v(-32.61, -71.4) * mm, "end": v(-37.5, -82.37) * mm});
            skLineSegment(sketch, "E46.9.26.0", {"start": v(-32.61, -71.4) * mm, "end": v(-31.24, -72.02) * mm});
            skLineSegment(sketch, "E46.2.27.0", {"start": v(-28.68, -85.84) * mm, "end": v(-27.25, -86.3) * mm});
            skLineSegment(sketch, "E46.3.27.0", {"start": v(-23.54, -74.89) * mm, "end": v(-27.25, -86.3) * mm});
            skLineSegment(sketch, "E46.6.27.0", {"start": v(-24.97, -74.43) * mm, "end": v(-28.68, -85.84) * mm});
            skLineSegment(sketch, "E46.9.27.0", {"start": v(-24.97, -74.43) * mm, "end": v(-23.54, -74.89) * mm});
            skLineSegment(sketch, "E46.2.28.0", {"start": v(-19.55, -88.37) * mm, "end": v(-18.08, -88.68) * mm});
            skLineSegment(sketch, "E46.3.28.0", {"start": v(-15.59, -76.94) * mm, "end": v(-18.08, -88.68) * mm});
            skLineSegment(sketch, "E46.6.28.0", {"start": v(-17.05, -76.63) * mm, "end": v(-19.55, -88.37) * mm});
            skLineSegment(sketch, "E46.9.28.0", {"start": v(-17.05, -76.63) * mm, "end": v(-15.59, -76.94) * mm});
            skLineSegment(sketch, "E46.2.29.0", {"start": v(-10.2, -89.93) * mm, "end": v(-8.71, -90.08) * mm});
            skLineSegment(sketch, "E46.3.29.0", {"start": v(-7.46, -78.15) * mm, "end": v(-8.71, -90.08) * mm});
            skLineSegment(sketch, "E46.6.29.0", {"start": v(-8.95, -78) * mm, "end": v(-10.2, -89.93) * mm});
            skLineSegment(sketch, "E46.9.29.0", {"start": v(-8.95, -78) * mm, "end": v(-7.46, -78.15) * mm});
            skLineSegment(sketch, "E46.2.30.0", {"start": v(-0.75, -90.5) * mm, "end": v(0.75, -90.5) * mm});
            skLineSegment(sketch, "E46.3.30.0", {"start": v(0.75, -78.5) * mm, "end": v(0.75, -90.5) * mm});
            skLineSegment(sketch, "E46.6.30.0", {"start": v(-0.75, -78.5) * mm, "end": v(-0.75, -90.5) * mm});
            skLineSegment(sketch, "E46.9.30.0", {"start": v(-0.75, -78.5) * mm, "end": v(0.75, -78.5) * mm});
            skLineSegment(sketch, "E46.2.31.0", {"start": v(8.71, -90.08) * mm, "end": v(10.2, -89.93) * mm});
            skLineSegment(sketch, "E46.3.31.0", {"start": v(8.95, -78) * mm, "end": v(10.2, -89.93) * mm});
            skLineSegment(sketch, "E46.6.31.0", {"start": v(7.46, -78.15) * mm, "end": v(8.71, -90.08) * mm});
            skLineSegment(sketch, "E46.9.31.0", {"start": v(7.46, -78.15) * mm, "end": v(8.95, -78) * mm});
            skLineSegment(sketch, "E46.2.32.0", {"start": v(18.08, -88.68) * mm, "end": v(19.55, -88.37) * mm});
            skLineSegment(sketch, "E46.3.32.0", {"start": v(17.05, -76.63) * mm, "end": v(19.55, -88.37) * mm});
            skLineSegment(sketch, "E46.6.32.0", {"start": v(15.59, -76.94) * mm, "end": v(18.08, -88.68) * mm});
            skLineSegment(sketch, "E46.9.32.0", {"start": v(15.59, -76.94) * mm, "end": v(17.05, -76.63) * mm});
            skLineSegment(sketch, "E46.2.33.0", {"start": v(27.25, -86.3) * mm, "end": v(28.68, -85.84) * mm});
            skLineSegment(sketch, "E46.3.33.0", {"start": v(24.97, -74.43) * mm, "end": v(28.68, -85.84) * mm});
            skLineSegment(sketch, "E46.6.33.0", {"start": v(23.54, -74.89) * mm, "end": v(27.25, -86.3) * mm});
            skLineSegment(sketch, "E46.9.33.0", {"start": v(23.54, -74.89) * mm, "end": v(24.97, -74.43) * mm});
            skLineSegment(sketch, "E46.2.34.0", {"start": v(36.12, -82.98) * mm, "end": v(37.5, -82.37) * mm});
            skLineSegment(sketch, "E46.3.34.0", {"start": v(32.61, -71.4) * mm, "end": v(37.5, -82.37) * mm});
            skLineSegment(sketch, "E46.6.34.0", {"start": v(31.24, -72.02) * mm, "end": v(36.12, -82.98) * mm});
            skLineSegment(sketch, "E46.9.34.0", {"start": v(31.24, -72.02) * mm, "end": v(32.61, -71.4) * mm});
            skLineSegment(sketch, "E46.2.35.0", {"start": v(44.6, -78.75) * mm, "end": v(45.9, -78) * mm});
            skLineSegment(sketch, "E46.3.35.0", {"start": v(39.9, -67.6) * mm, "end": v(45.9, -78) * mm});
            skLineSegment(sketch, "E46.6.35.0", {"start": v(38.6, -68.36) * mm, "end": v(44.6, -78.75) * mm});
            skLineSegment(sketch, "E46.9.35.0", {"start": v(38.6, -68.36) * mm, "end": v(39.9, -67.6) * mm});
            skLineSegment(sketch, "E46.2.36.0", {"start": v(52.59, -73.66) * mm, "end": v(53.8, -72.78) * mm});
            skLineSegment(sketch, "E46.3.36.0", {"start": v(46.75, -63.07) * mm, "end": v(53.8, -72.78) * mm});
            skLineSegment(sketch, "E46.6.36.0", {"start": v(45.53, -63.95) * mm, "end": v(52.59, -73.66) * mm});
            skLineSegment(sketch, "E46.9.36.0", {"start": v(45.53, -63.95) * mm, "end": v(46.75, -63.07) * mm});
            skLineSegment(sketch, "E46.2.37.0", {"start": v(60, -67.76) * mm, "end": v(61.11, -66.75) * mm});
            skLineSegment(sketch, "E46.3.37.0", {"start": v(53.08, -57.84) * mm, "end": v(61.11, -66.75) * mm});
            skLineSegment(sketch, "E46.6.37.0", {"start": v(51.97, -58.84) * mm, "end": v(60, -67.76) * mm});
            skLineSegment(sketch, "E46.9.37.0", {"start": v(51.97, -58.84) * mm, "end": v(53.08, -57.84) * mm});
            skLineSegment(sketch, "E46.2.38.0", {"start": v(66.75, -61.11) * mm, "end": v(67.76, -60) * mm});
            skLineSegment(sketch, "E46.3.38.0", {"start": v(58.84, -51.97) * mm, "end": v(67.76, -60) * mm});
            skLineSegment(sketch, "E46.6.38.0", {"start": v(57.84, -53.08) * mm, "end": v(66.75, -61.11) * mm});
            skLineSegment(sketch, "E46.9.38.0", {"start": v(57.84, -53.08) * mm, "end": v(58.84, -51.97) * mm});
            skLineSegment(sketch, "E46.2.39.0", {"start": v(72.78, -53.8) * mm, "end": v(73.66, -52.59) * mm});
            skLineSegment(sketch, "E46.3.39.0", {"start": v(63.95, -45.53) * mm, "end": v(73.66, -52.59) * mm});
            skLineSegment(sketch, "E46.6.39.0", {"start": v(63.07, -46.75) * mm, "end": v(72.78, -53.8) * mm});
            skLineSegment(sketch, "E46.9.39.0", {"start": v(63.07, -46.75) * mm, "end": v(63.95, -45.53) * mm});
            skLineSegment(sketch, "E46.2.40.0", {"start": v(78, -45.9) * mm, "end": v(78.75, -44.6) * mm});
            skLineSegment(sketch, "E46.3.40.0", {"start": v(68.36, -38.6) * mm, "end": v(78.75, -44.6) * mm});
            skLineSegment(sketch, "E46.6.40.0", {"start": v(67.6, -39.9) * mm, "end": v(78, -45.9) * mm});
            skLineSegment(sketch, "E46.9.40.0", {"start": v(67.6, -39.9) * mm, "end": v(68.36, -38.6) * mm});
            skLineSegment(sketch, "E46.2.41.0", {"start": v(82.37, -37.5) * mm, "end": v(82.98, -36.12) * mm});
            skLineSegment(sketch, "E46.3.41.0", {"start": v(72.02, -31.24) * mm, "end": v(82.98, -36.12) * mm});
            skLineSegment(sketch, "E46.6.41.0", {"start": v(71.4, -32.61) * mm, "end": v(82.37, -37.5) * mm});
            skLineSegment(sketch, "E46.9.41.0", {"start": v(71.4, -32.61) * mm, "end": v(72.02, -31.24) * mm});
            skLineSegment(sketch, "E46.2.42.0", {"start": v(85.84, -28.68) * mm, "end": v(86.3, -27.25) * mm});
            skLineSegment(sketch, "E46.3.42.0", {"start": v(74.89, -23.54) * mm, "end": v(86.3, -27.25) * mm});
            skLineSegment(sketch, "E46.6.42.0", {"start": v(74.43, -24.97) * mm, "end": v(85.84, -28.68) * mm});
            skLineSegment(sketch, "E46.9.42.0", {"start": v(74.43, -24.97) * mm, "end": v(74.89, -23.54) * mm});
            skLineSegment(sketch, "E46.2.43.0", {"start": v(88.37, -19.55) * mm, "end": v(88.68, -18.08) * mm});
            skLineSegment(sketch, "E46.3.43.0", {"start": v(76.94, -15.59) * mm, "end": v(88.68, -18.08) * mm});
            skLineSegment(sketch, "E46.6.43.0", {"start": v(76.63, -17.05) * mm, "end": v(88.37, -19.55) * mm});
            skLineSegment(sketch, "E46.9.43.0", {"start": v(76.63, -17.05) * mm, "end": v(76.94, -15.59) * mm});
            skLineSegment(sketch, "E46.2.44.0", {"start": v(89.93, -10.2) * mm, "end": v(90.08, -8.71) * mm});
            skLineSegment(sketch, "E46.3.44.0", {"start": v(78.15, -7.46) * mm, "end": v(90.08, -8.71) * mm});
            skLineSegment(sketch, "E46.6.44.0", {"start": v(78, -8.95) * mm, "end": v(89.93, -10.2) * mm});
            skLineSegment(sketch, "E46.9.44.0", {"start": v(78, -8.95) * mm, "end": v(78.15, -7.46) * mm});
            skLineSegment(sketch, "E46.2.45.0", {"start": v(90.5, -0.75) * mm, "end": v(90.5, 0.75) * mm});
            skLineSegment(sketch, "E46.3.45.0", {"start": v(78.5, 0.75) * mm, "end": v(90.5, 0.75) * mm});
            skLineSegment(sketch, "E46.6.45.0", {"start": v(78.5, -0.75) * mm, "end": v(90.5, -0.75) * mm});
            skLineSegment(sketch, "E46.9.45.0", {"start": v(78.5, -0.75) * mm, "end": v(78.5, 0.75) * mm});
            skLineSegment(sketch, "E46.2.46.0", {"start": v(90.08, 8.71) * mm, "end": v(89.93, 10.2) * mm});
            skLineSegment(sketch, "E46.3.46.0", {"start": v(78, 8.95) * mm, "end": v(89.93, 10.2) * mm});
            skLineSegment(sketch, "E46.6.46.0", {"start": v(78.15, 7.46) * mm, "end": v(90.08, 8.71) * mm});
            skLineSegment(sketch, "E46.9.46.0", {"start": v(78.15, 7.46) * mm, "end": v(78, 8.95) * mm});
            skLineSegment(sketch, "E46.2.47.0", {"start": v(88.68, 18.08) * mm, "end": v(88.37, 19.55) * mm});
            skLineSegment(sketch, "E46.3.47.0", {"start": v(76.63, 17.05) * mm, "end": v(88.37, 19.55) * mm});
            skLineSegment(sketch, "E46.6.47.0", {"start": v(76.94, 15.59) * mm, "end": v(88.68, 18.08) * mm});
            skLineSegment(sketch, "E46.9.47.0", {"start": v(76.94, 15.59) * mm, "end": v(76.63, 17.05) * mm});
            skLineSegment(sketch, "E46.2.48.0", {"start": v(86.3, 27.25) * mm, "end": v(85.84, 28.68) * mm});
            skLineSegment(sketch, "E46.3.48.0", {"start": v(74.43, 24.97) * mm, "end": v(85.84, 28.68) * mm});
            skLineSegment(sketch, "E46.6.48.0", {"start": v(74.89, 23.54) * mm, "end": v(86.3, 27.25) * mm});
            skLineSegment(sketch, "E46.9.48.0", {"start": v(74.89, 23.54) * mm, "end": v(74.43, 24.97) * mm});
            skLineSegment(sketch, "E46.2.49.0", {"start": v(82.98, 36.12) * mm, "end": v(82.37, 37.5) * mm});
            skLineSegment(sketch, "E46.3.49.0", {"start": v(71.4, 32.61) * mm, "end": v(82.37, 37.5) * mm});
            skLineSegment(sketch, "E46.6.49.0", {"start": v(72.02, 31.24) * mm, "end": v(82.98, 36.12) * mm});
            skLineSegment(sketch, "E46.9.49.0", {"start": v(72.02, 31.24) * mm, "end": v(71.4, 32.61) * mm});
            skLineSegment(sketch, "E46.2.50.0", {"start": v(78.75, 44.6) * mm, "end": v(78, 45.9) * mm});
            skLineSegment(sketch, "E46.3.50.0", {"start": v(67.6, 39.9) * mm, "end": v(78, 45.9) * mm});
            skLineSegment(sketch, "E46.6.50.0", {"start": v(68.36, 38.6) * mm, "end": v(78.75, 44.6) * mm});
            skLineSegment(sketch, "E46.9.50.0", {"start": v(68.36, 38.6) * mm, "end": v(67.6, 39.9) * mm});
            skLineSegment(sketch, "E46.2.51.0", {"start": v(73.66, 52.59) * mm, "end": v(72.78, 53.8) * mm});
            skLineSegment(sketch, "E46.3.51.0", {"start": v(63.07, 46.75) * mm, "end": v(72.78, 53.8) * mm});
            skLineSegment(sketch, "E46.6.51.0", {"start": v(63.95, 45.53) * mm, "end": v(73.66, 52.59) * mm});
            skLineSegment(sketch, "E46.9.51.0", {"start": v(63.95, 45.53) * mm, "end": v(63.07, 46.75) * mm});
            skLineSegment(sketch, "E46.2.52.0", {"start": v(67.76, 60) * mm, "end": v(66.75, 61.11) * mm});
            skLineSegment(sketch, "E46.3.52.0", {"start": v(57.84, 53.08) * mm, "end": v(66.75, 61.11) * mm});
            skLineSegment(sketch, "E46.6.52.0", {"start": v(58.84, 51.97) * mm, "end": v(67.76, 60) * mm});
            skLineSegment(sketch, "E46.9.52.0", {"start": v(58.84, 51.97) * mm, "end": v(57.84, 53.08) * mm});
            skLineSegment(sketch, "E46.2.53.0", {"start": v(61.11, 66.75) * mm, "end": v(60, 67.76) * mm});
            skLineSegment(sketch, "E46.3.53.0", {"start": v(51.97, 58.84) * mm, "end": v(60, 67.76) * mm});
            skLineSegment(sketch, "E46.6.53.0", {"start": v(53.08, 57.84) * mm, "end": v(61.11, 66.75) * mm});
            skLineSegment(sketch, "E46.9.53.0", {"start": v(53.08, 57.84) * mm, "end": v(51.97, 58.84) * mm});
            skLineSegment(sketch, "E46.2.54.0", {"start": v(53.8, 72.78) * mm, "end": v(52.59, 73.66) * mm});
            skLineSegment(sketch, "E46.3.54.0", {"start": v(45.53, 63.95) * mm, "end": v(52.59, 73.66) * mm});
            skLineSegment(sketch, "E46.6.54.0", {"start": v(46.75, 63.07) * mm, "end": v(53.8, 72.78) * mm});
            skLineSegment(sketch, "E46.9.54.0", {"start": v(46.75, 63.07) * mm, "end": v(45.53, 63.95) * mm});
            skLineSegment(sketch, "E46.2.55.0", {"start": v(45.9, 78) * mm, "end": v(44.6, 78.75) * mm});
            skLineSegment(sketch, "E46.3.55.0", {"start": v(38.6, 68.36) * mm, "end": v(44.6, 78.75) * mm});
            skLineSegment(sketch, "E46.6.55.0", {"start": v(39.9, 67.6) * mm, "end": v(45.9, 78) * mm});
            skLineSegment(sketch, "E46.9.55.0", {"start": v(39.9, 67.6) * mm, "end": v(38.6, 68.36) * mm});
            skLineSegment(sketch, "E46.2.56.0", {"start": v(37.5, 82.37) * mm, "end": v(36.12, 82.98) * mm});
            skLineSegment(sketch, "E46.3.56.0", {"start": v(31.24, 72.02) * mm, "end": v(36.12, 82.98) * mm});
            skLineSegment(sketch, "E46.6.56.0", {"start": v(32.61, 71.4) * mm, "end": v(37.5, 82.37) * mm});
            skLineSegment(sketch, "E46.9.56.0", {"start": v(32.61, 71.4) * mm, "end": v(31.24, 72.02) * mm});
            skLineSegment(sketch, "E46.2.57.0", {"start": v(28.68, 85.84) * mm, "end": v(27.25, 86.3) * mm});
            skLineSegment(sketch, "E46.3.57.0", {"start": v(23.54, 74.89) * mm, "end": v(27.25, 86.3) * mm});
            skLineSegment(sketch, "E46.6.57.0", {"start": v(24.97, 74.43) * mm, "end": v(28.68, 85.84) * mm});
            skLineSegment(sketch, "E46.9.57.0", {"start": v(24.97, 74.43) * mm, "end": v(23.54, 74.89) * mm});
            skLineSegment(sketch, "E46.2.58.0", {"start": v(19.55, 88.37) * mm, "end": v(18.08, 88.68) * mm});
            skLineSegment(sketch, "E46.3.58.0", {"start": v(15.59, 76.94) * mm, "end": v(18.08, 88.68) * mm});
            skLineSegment(sketch, "E46.6.58.0", {"start": v(17.05, 76.63) * mm, "end": v(19.55, 88.37) * mm});
            skLineSegment(sketch, "E46.9.58.0", {"start": v(17.05, 76.63) * mm, "end": v(15.59, 76.94) * mm});
            skLineSegment(sketch, "E46.2.59.0", {"start": v(10.2, 89.93) * mm, "end": v(8.71, 90.08) * mm});
            skLineSegment(sketch, "E46.3.59.0", {"start": v(7.46, 78.15) * mm, "end": v(8.71, 90.08) * mm});
            skLineSegment(sketch, "E46.6.59.0", {"start": v(8.95, 78) * mm, "end": v(10.2, 89.93) * mm});
            skLineSegment(sketch, "E46.9.59.0", {"start": v(8.95, 78) * mm, "end": v(7.46, 78.15) * mm});
            skSolve(sketch);
        }
        {
            var Q0;
            Q0 = qSketchRegion(id + "F27", true);
            extrude(context, id + "F28", {"entities" : qUnion([Q0]), "operationType" : NewBodyOperationType.REMOVE, "oppositeDirection" : true, "depth" : 0.2 * mm, "offsetDistance" : 25 * mm});
        }
        {
            var Q0;
            Q0=makeQuery(id+"F26.boolean.opBoolean","COPY",FACE,{"derivedFrom":makeQuery(id+"F26.opExtrude","CAP_FACE",FACE,{"disambiguationData":[OSD([sQuery(id+"F25.wireOp",EDGE,"E41.bottom"),sQuery(id+"F25.wireOp",EDGE,"E41.top"),sQuery(id+"F25.wireOp",EDGE,"E41.left"),sQuery(id+"F25.wireOp",EDGE,"E41.right")])],"isStart":false})});
            extrude(context, id + "F29", {"entities" : qUnion([Q0]), "depth" : 1 * mm, "offsetDistance" : 25 * mm});
        }
        {
            var Q0;
            Q0=makeQuery(id+"F28.boolean.opBoolean","COPY",FACE,{"derivedFrom":makeQuery(id+"F28.opExtrude","CAP_FACE",FACE,{"disambiguationData":[OSD([sQuery(id+"F27.wireOp",EDGE,"E46.2.59.0"),sQuery(id+"F27.wireOp",EDGE,"E46.3.59.0"),sQuery(id+"F27.wireOp",EDGE,"E46.6.59.0"),sQuery(id+"F27.wireOp",EDGE,"E46.9.59.0")])],"isStart":false})});
            extrude(context, id + "F30", {"entities" : qUnion([Q0]), "depth" : 0.4 * mm, "offsetDistance" : 25 * mm});
        }
        {
            var Q0;
            Q0=makeQuery(id+"F15.opExtrude","CAP_FACE",FACE,{"disambiguationData":[OSD([sQuery(id+"F14.wireOp",EDGE,"E21.0"),sQuery(id+"F14.wireOp",EDGE,"E22"),sQuery(id+"F14.wireOp",EDGE,"E23"),sQuery(id+"F14.wireOp",EDGE,"E24"),sQuery(id+"F14.wireOp",EDGE,"E25.MirrorCS"),sQuery(id+"F14.wireOp",EDGE,"E26.MirrorCS"),sQuery(id+"F14.wireOp",EDGE,"E27.1.0"),sQuery(id+"F14.wireOp",EDGE,"E27.1.1"),sQuery(id+"F14.wireOp",EDGE,"E27.1.2"),sQuery(id+"F14.wireOp",EDGE,"E27.1.3"),sQuery(id+"F14.wireOp",EDGE,"E27.2.0"),sQuery(id+"F14.wireOp",EDGE,"E27.2.1"),sQuery(id+"F14.wireOp",EDGE,"E27.2.2"),sQuery(id+"F14.wireOp",EDGE,"E27.2.3"),sQuery(id+"F14.wireOp",EDGE,"E28.2.3.0"),sQuery(id+"F14.wireOp",EDGE,"E28.3.3.0"),sQuery(id+"F14.wireOp",EDGE,"E28.6.3.0"),sQuery(id+"F14.wireOp",EDGE,"E28.9.3.0"),sQuery(id+"F14.wireOp",EDGE,"E28.2.4.0"),sQuery(id+"F14.wireOp",EDGE,"E28.3.4.0"),sQuery(id+"F14.wireOp",EDGE,"E28.6.4.0"),sQuery(id+"F14.wireOp",EDGE,"E28.9.4.0"),sQuery(id+"F14.wireOp",EDGE,"E28.2.5.0"),sQuery(id+"F14.wireOp",EDGE,"E28.3.5.0"),sQuery(id+"F14.wireOp",EDGE,"E28.6.5.0"),sQuery(id+"F14.wireOp",EDGE,"E28.9.5.0"),sQuery(id+"F14.wireOp",EDGE,"E28.2.6.0"),sQuery(id+"F14.wireOp",EDGE,"E28.3.6.0"),sQuery(id+"F14.wireOp",EDGE,"E28.6.6.0"),sQuery(id+"F14.wireOp",EDGE,"E28.9.6.0"),sQuery(id+"F14.wireOp",EDGE,"E28.2.7.0"),sQuery(id+"F14.wireOp",EDGE,"E28.3.7.0"),sQuery(id+"F14.wireOp",EDGE,"E28.6.7.0"),sQuery(id+"F14.wireOp",EDGE,"E28.9.7.0"),sQuery(id+"F14.wireOp",EDGE,"E28.2.8.0"),sQuery(id+"F14.wireOp",EDGE,"E28.3.8.0"),sQuery(id+"F14.wireOp",EDGE,"E28.6.8.0"),sQuery(id+"F14.wireOp",EDGE,"E28.9.8.0"),sQuery(id+"F14.wireOp",EDGE,"E28.2.9.0"),sQuery(id+"F14.wireOp",EDGE,"E28.3.9.0"),sQuery(id+"F14.wireOp",EDGE,"E28.6.9.0"),sQuery(id+"F14.wireOp",EDGE,"E28.9.9.0"),sQuery(id+"F14.wireOp",EDGE,"E28.2.10.0"),sQuery(id+"F14.wireOp",EDGE,"E28.3.10.0"),sQuery(id+"F14.wireOp",EDGE,"E28.6.10.0"),sQuery(id+"F14.wireOp",EDGE,"E28.9.10.0"),sQuery(id+"F14.wireOp",EDGE,"E28.2.11.0"),sQuery(id+"F14.wireOp",EDGE,"E28.3.11.0"),sQuery(id+"F14.wireOp",EDGE,"E28.6.11.0"),sQuery(id+"F14.wireOp",EDGE,"E28.9.11.0"),sQuery(id+"F14.wireOp",EDGE,"E28.2.12.0"),sQuery(id+"F14.wireOp",EDGE,"E28.3.12.0"),sQuery(id+"F14.wireOp",EDGE,"E28.6.12.0"),sQuery(id+"F14.wireOp",EDGE,"E28.9.12.0"),sQuery(id+"F14.wireOp",EDGE,"E28.2.13.0"),sQuery(id+"F14.wireOp",EDGE,"E28.3.13.0"),sQuery(id+"F14.wireOp",EDGE,"E28.6.13.0"),sQuery(id+"F14.wireOp",EDGE,"E28.9.13.0"),sQuery(id+"F14.wireOp",EDGE,"E28.2.14.0"),sQuery(id+"F14.wireOp",EDGE,"E28.3.14.0"),sQuery(id+"F14.wireOp",EDGE,"E28.6.14.0"),sQuery(id+"F14.wireOp",EDGE,"E28.9.14.0"),sQuery(id+"F14.wireOp",EDGE,"E28.2.15.0"),sQuery(id+"F14.wireOp",EDGE,"E28.3.15.0"),sQuery(id+"F14.wireOp",EDGE,"E28.6.15.0"),sQuery(id+"F14.wireOp",EDGE,"E28.9.15.0"),sQuery(id+"F14.wireOp",EDGE,"E28.2.16.0"),sQuery(id+"F14.wireOp",EDGE,"E28.3.16.0"),sQuery(id+"F14.wireOp",EDGE,"E28.6.16.0"),sQuery(id+"F14.wireOp",EDGE,"E28.9.16.0"),sQuery(id+"F14.wireOp",EDGE,"E28.2.17.0"),sQuery(id+"F14.wireOp",EDGE,"E28.3.17.0"),sQuery(id+"F14.wireOp",EDGE,"E28.6.17.0"),sQuery(id+"F14.wireOp",EDGE,"E28.9.17.0"),sQuery(id+"F14.wireOp",EDGE,"E28.2.18.0"),sQuery(id+"F14.wireOp",EDGE,"E28.3.18.0"),sQuery(id+"F14.wireOp",EDGE,"E28.6.18.0"),sQuery(id+"F14.wireOp",EDGE,"E28.9.18.0"),sQuery(id+"F14.wireOp",EDGE,"E28.2.19.0"),sQuery(id+"F14.wireOp",EDGE,"E28.3.19.0"),sQuery(id+"F14.wireOp",EDGE,"E28.6.19.0"),sQuery(id+"F14.wireOp",EDGE,"E28.9.19.0"),sQuery(id+"F14.wireOp",EDGE,"E28.2.20.0"),sQuery(id+"F14.wireOp",EDGE,"E28.3.20.0"),sQuery(id+"F14.wireOp",EDGE,"E28.6.20.0"),sQuery(id+"F14.wireOp",EDGE,"E28.9.20.0"),sQuery(id+"F14.wireOp",EDGE,"E28.2.21.0"),sQuery(id+"F14.wireOp",EDGE,"E28.3.21.0"),sQuery(id+"F14.wireOp",EDGE,"E28.6.21.0"),sQuery(id+"F14.wireOp",EDGE,"E28.9.21.0"),sQuery(id+"F14.wireOp",EDGE,"E28.2.22.0"),sQuery(id+"F14.wireOp",EDGE,"E28.3.22.0"),sQuery(id+"F14.wireOp",EDGE,"E28.6.22.0"),sQuery(id+"F14.wireOp",EDGE,"E28.9.22.0"),sQuery(id+"F14.wireOp",EDGE,"E28.2.23.0"),sQuery(id+"F14.wireOp",EDGE,"E28.3.23.0"),sQuery(id+"F14.wireOp",EDGE,"E28.6.23.0"),sQuery(id+"F14.wireOp",EDGE,"E28.9.23.0"),sQuery(id+"F14.wireOp",EDGE,"E28.2.24.0"),sQuery(id+"F14.wireOp",EDGE,"E28.3.24.0"),sQuery(id+"F14.wireOp",EDGE,"E28.6.24.0"),sQuery(id+"F14.wireOp",EDGE,"E28.9.24.0"),sQuery(id+"F14.wireOp",EDGE,"E28.2.25.0"),sQuery(id+"F14.wireOp",EDGE,"E28.3.25.0"),sQuery(id+"F14.wireOp",EDGE,"E28.6.25.0"),sQuery(id+"F14.wireOp",EDGE,"E28.9.25.0"),sQuery(id+"F14.wireOp",EDGE,"E28.2.26.0"),sQuery(id+"F14.wireOp",EDGE,"E28.3.26.0"),sQuery(id+"F14.wireOp",EDGE,"E28.6.26.0"),sQuery(id+"F14.wireOp",EDGE,"E28.9.26.0"),sQuery(id+"F14.wireOp",EDGE,"E28.2.27.0"),sQuery(id+"F14.wireOp",EDGE,"E28.3.27.0"),sQuery(id+"F14.wireOp",EDGE,"E28.6.27.0"),sQuery(id+"F14.wireOp",EDGE,"E28.9.27.0"),sQuery(id+"F14.wireOp",EDGE,"E28.2.28.0"),sQuery(id+"F14.wireOp",EDGE,"E28.3.28.0"),sQuery(id+"F14.wireOp",EDGE,"E28.6.28.0"),sQuery(id+"F14.wireOp",EDGE,"E28.9.28.0"),sQuery(id+"F14.wireOp",EDGE,"E28.2.29.0"),sQuery(id+"F14.wireOp",EDGE,"E28.3.29.0"),sQuery(id+"F14.wireOp",EDGE,"E28.6.29.0"),sQuery(id+"F14.wireOp",EDGE,"E28.9.29.0"),sQuery(id+"F14.wireOp",EDGE,"E28.2.30.0"),sQuery(id+"F14.wireOp",EDGE,"E28.3.30.0"),sQuery(id+"F14.wireOp",EDGE,"E28.6.30.0"),sQuery(id+"F14.wireOp",EDGE,"E28.9.30.0"),sQuery(id+"F14.wireOp",EDGE,"E28.2.31.0"),sQuery(id+"F14.wireOp",EDGE,"E28.3.31.0"),sQuery(id+"F14.wireOp",EDGE,"E28.6.31.0"),sQuery(id+"F14.wireOp",EDGE,"E28.9.31.0"),sQuery(id+"F14.wireOp",EDGE,"E28.2.32.0"),sQuery(id+"F14.wireOp",EDGE,"E28.3.32.0"),sQuery(id+"F14.wireOp",EDGE,"E28.6.32.0"),sQuery(id+"F14.wireOp",EDGE,"E28.9.32.0"),sQuery(id+"F14.wireOp",EDGE,"E28.2.33.0"),sQuery(id+"F14.wireOp",EDGE,"E28.3.33.0"),sQuery(id+"F14.wireOp",EDGE,"E28.6.33.0"),sQuery(id+"F14.wireOp",EDGE,"E28.9.33.0"),sQuery(id+"F14.wireOp",EDGE,"E28.2.34.0"),sQuery(id+"F14.wireOp",EDGE,"E28.3.34.0"),sQuery(id+"F14.wireOp",EDGE,"E28.6.34.0"),sQuery(id+"F14.wireOp",EDGE,"E28.9.34.0"),sQuery(id+"F14.wireOp",EDGE,"E28.2.35.0"),sQuery(id+"F14.wireOp",EDGE,"E28.3.35.0"),sQuery(id+"F14.wireOp",EDGE,"E28.6.35.0"),sQuery(id+"F14.wireOp",EDGE,"E28.9.35.0"),sQuery(id+"F14.wireOp",EDGE,"E28.2.36.0"),sQuery(id+"F14.wireOp",EDGE,"E28.3.36.0"),sQuery(id+"F14.wireOp",EDGE,"E28.6.36.0"),sQuery(id+"F14.wireOp",EDGE,"E28.9.36.0"),sQuery(id+"F14.wireOp",EDGE,"E28.2.37.0"),sQuery(id+"F14.wireOp",EDGE,"E28.3.37.0"),sQuery(id+"F14.wireOp",EDGE,"E28.6.37.0"),sQuery(id+"F14.wireOp",EDGE,"E28.9.37.0"),sQuery(id+"F14.wireOp",EDGE,"E28.2.38.0"),sQuery(id+"F14.wireOp",EDGE,"E28.3.38.0"),sQuery(id+"F14.wireOp",EDGE,"E28.6.38.0"),sQuery(id+"F14.wireOp",EDGE,"E28.9.38.0"),sQuery(id+"F14.wireOp",EDGE,"E28.2.39.0"),sQuery(id+"F14.wireOp",EDGE,"E28.3.39.0"),sQuery(id+"F14.wireOp",EDGE,"E28.6.39.0"),sQuery(id+"F14.wireOp",EDGE,"E28.9.39.0")])],"isStart":false});
            var sketch = newSketch(context, id + "F31", { "sketchPlane" : qUnion([Q0])});
            skCircle(sketch, "E47.0", {"center": v(0, 0) * mm, "radius": 3 * mm});
            skCircle(sketch, "E48.0", {"center": v(0, 0) * mm, "radius": 5 * mm});
            skSolve(sketch);
        }
        {
            var Q0;
            Q0 = qSketchRegion(id + "F31", true);
            extrude(context, id + "F32", {"entities" : qUnion([Q0]), "operationType" : NewBodyOperationType.ADD, "depth" : 5 * mm, "offsetDistance" : 25 * mm});
        }
        {
            var Q0;
            Q0=makeQuery(id+"F32.opExtrude","CAP_FACE",FACE,{"disambiguationData":[OSD([sQuery(id+"F31.wireOp",EDGE,"E47.0"),sQuery(id+"F31.wireOp",EDGE,"E48.0")])],"isStart":false});
            var sketch = newSketch(context, id + "F33", { "sketchPlane" : qUnion([Q0])});
            skCircle(sketch, "E49.0", {"center": v(0, 0) * mm, "radius": 3 * mm});
            skCircle(sketch, "E50.0", {"center": v(0, 0) * mm, "radius": 5 * mm});
            skLineSegment(sketch, "E51", {"start": v(0, 50) * mm, "end": v(1.5, 50) * mm});
            skLineSegment(sketch, "E52", {"start": v(1.5, 50) * mm, "end": v(3, 4) * mm});
            skLineSegment(sketch, "E53.MirrorCS", {"start": v(0, 50) * mm, "end": v(-1.5, 50) * mm});
            skLineSegment(sketch, "E54.MirrorCS", {"start": v(-1.5, 50) * mm, "end": v(-3, 4) * mm});
            skSolve(sketch);
        }
        {
            var Q0;
            Q0 = qSketchRegion(id + "F33", true);
            extrude(context, id + "F34", {"entities" : qUnion([Q0]), "operationType" : NewBodyOperationType.ADD, "depth" : 1 * mm, "offsetDistance" : 25 * mm});
        }
        {
            var Q0;
            Q0=makeQuery(id+"F6.opExtrude","CAP_FACE",FACE,{"disambiguationData":[OSD([sQuery(id+"F0.wireOp",EDGE,"E0")])],"isStart":false});
            var sketch = newSketch(context, id + "F35", { "sketchPlane" : qUnion([Q0])});
            skCircle(sketch, "E55", {"center": v(0, 0) * mm, "radius": 5 * mm});
            skLineSegment(sketch, "E56", {"start": v(0, 80) * mm, "end": v(0.5, 80) * mm});
            skLineSegment(sketch, "E57", {"start": v(0.5, 80) * mm, "end": v(2, 4.58) * mm});
            skLineSegment(sketch, "E58.MirrorCS", {"start": v(0, 80) * mm, "end": v(-0.5, 80) * mm});
            skLineSegment(sketch, "E59.MirrorCS", {"start": v(-0.5, 80) * mm, "end": v(-2, 4.58) * mm});
            skSolve(sketch);
        }
        {
            var Q0;
            Q0 = qSketchRegion(id + "F35", true);
            extrude(context, id + "F36", {"entities" : qUnion([Q0]), "operationType" : NewBodyOperationType.ADD, "oppositeDirection" : true, "depth" : 1 * mm, "offsetDistance" : 25 * mm});
        }
    });
